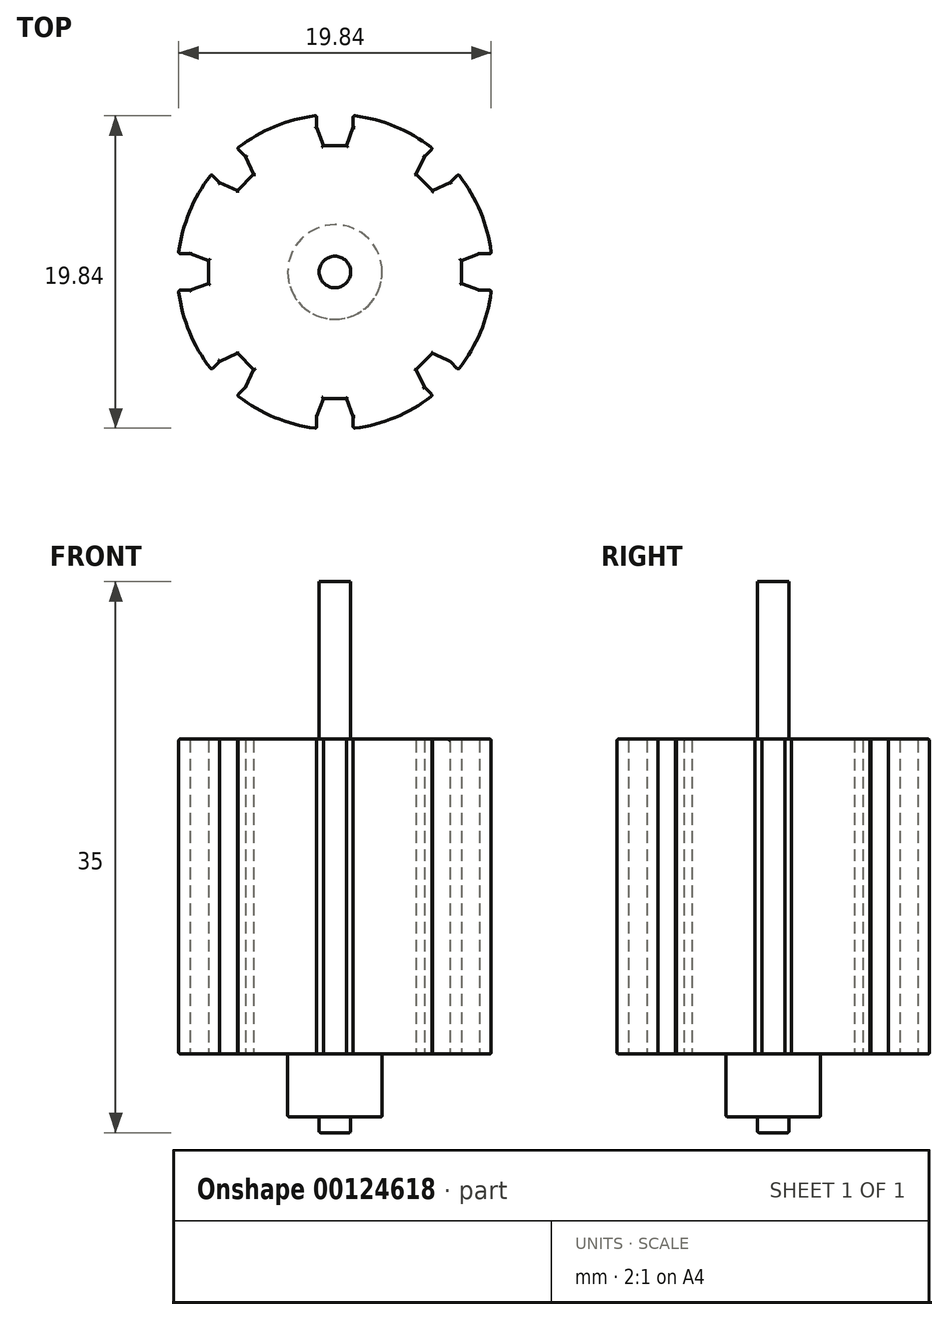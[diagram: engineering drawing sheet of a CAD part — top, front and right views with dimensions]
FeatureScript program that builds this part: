
annotation { "Feature Type Name" : "Feature", "Feature Type Description" : "" }
export const myFeature = defineFeature(function(context is Context, id is Id, definition is map)
    precondition{}
    {
        {
            var Q0;
            Q0=qCreatedBy(makeId("Top.planeOp"),FACE);
            var sketch = newSketch(context, id + "F0", { "sketchPlane" : qUnion([Q0])});
            skCircle(sketch, "E0", {"center": v(0, 0) * mm, "radius": 1 * mm});
            skSolve(sketch);
        }
        {
            var Q0;
            Q0=makeQuery(id+"F0.imprint","IMPRINT",FACE,{"disambiguationData":[TD([[makeQuery(id+"F0.imprint","IMPRINT",EDGE,{"derivedFrom":sQuery(id+"F0.wireOp",EDGE,"E0")}),1.0]])]});
            extrude(context, id + "F1", {"entities" : qUnion([Q0]), "depth" : 30 * mm});
        }
        {
            var Q0;
            Q0=qCreatedBy(makeId("Top.planeOp"),FACE);
            cPlane(context, id + "F2", {"entities" : qUnion([Q0]), "cplaneType" : CPlaneType.OFFSET, "offset" : 15 * mm, "width" : 150 * mm, "height" : 150 * mm});
        }
        {
            var Q0;
            Q0=qCreatedBy(id+"F2.planeOp",FACE);
            var sketch = newSketch(context, id + "F3", { "sketchPlane" : qUnion([Q0])});
            skCircle(sketch, "E1", {"center": v(0, 0) * mm, "radius": 10 * mm});
            skLineSegment(sketch, "E2", {"start": v(0, 10) * mm, "end": v(0, 8.03) * mm});
            skLineSegment(sketch, "E3", {"start": v(0, 8.03) * mm, "end": v(0.73, 8.03) * mm});
            skLineSegment(sketch, "E4", {"start": v(0.73, 8.03) * mm, "end": v(1.42, 9.9) * mm});
            skLineSegment(sketch, "E5", {"start": v(0, 8.03) * mm, "end": v(-0.73, 8.03) * mm});
            skLineSegment(sketch, "E6", {"start": v(-0.73, 8.03) * mm, "end": v(-1.42, 9.9) * mm});
            skLineSegment(sketch, "E7", {"start": v(1.16, 9.93) * mm, "end": v(1.16, 9.2) * mm});
            skLineSegment(sketch, "E8", {"start": v(-1.16, 9.93) * mm, "end": v(-1.16, 9.2) * mm});
            skLineSegment(sketch, "E9.1.0", {"start": v(-7.84, 6.2) * mm, "end": v(-7.32, 5.68) * mm});
            skLineSegment(sketch, "E9.1.1", {"start": v(-6.2, 5.16) * mm, "end": v(-8, 6) * mm});
            skLineSegment(sketch, "E9.1.2", {"start": v(-5.68, 5.68) * mm, "end": v(-6.2, 5.16) * mm});
            skLineSegment(sketch, "E9.1.3", {"start": v(-5.68, 5.68) * mm, "end": v(-5.16, 6.2) * mm});
            skLineSegment(sketch, "E9.1.4", {"start": v(-5.16, 6.2) * mm, "end": v(-6, 8) * mm});
            skLineSegment(sketch, "E9.1.5", {"start": v(-6.2, 7.84) * mm, "end": v(-5.68, 7.32) * mm});
            skLineSegment(sketch, "E9.2.0", {"start": v(-9.93, -1.16) * mm, "end": v(-9.2, -1.16) * mm});
            skLineSegment(sketch, "E9.2.1", {"start": v(-8.03, -0.73) * mm, "end": v(-9.9, -1.42) * mm});
            skLineSegment(sketch, "E9.2.2", {"start": v(-8.03, 0) * mm, "end": v(-8.03, -0.73) * mm});
            skLineSegment(sketch, "E9.2.3", {"start": v(-8.03, 0) * mm, "end": v(-8.03, 0.73) * mm});
            skLineSegment(sketch, "E9.2.4", {"start": v(-8.03, 0.73) * mm, "end": v(-9.9, 1.42) * mm});
            skLineSegment(sketch, "E9.2.5", {"start": v(-9.93, 1.16) * mm, "end": v(-9.2, 1.16) * mm});
            skLineSegment(sketch, "E9.3.0", {"start": v(-6.2, -7.84) * mm, "end": v(-5.68, -7.32) * mm});
            skLineSegment(sketch, "E9.3.1", {"start": v(-5.16, -6.2) * mm, "end": v(-6, -8) * mm});
            skLineSegment(sketch, "E9.3.2", {"start": v(-5.68, -5.68) * mm, "end": v(-5.16, -6.2) * mm});
            skLineSegment(sketch, "E9.3.3", {"start": v(-5.68, -5.68) * mm, "end": v(-6.2, -5.16) * mm});
            skLineSegment(sketch, "E9.3.4", {"start": v(-6.2, -5.16) * mm, "end": v(-8, -6) * mm});
            skLineSegment(sketch, "E9.3.5", {"start": v(-7.84, -6.2) * mm, "end": v(-7.32, -5.68) * mm});
            skLineSegment(sketch, "E9.4.0", {"start": v(1.16, -9.93) * mm, "end": v(1.16, -9.2) * mm});
            skLineSegment(sketch, "E9.4.1", {"start": v(0.73, -8.03) * mm, "end": v(1.42, -9.9) * mm});
            skLineSegment(sketch, "E9.4.2", {"start": v(0, -8.03) * mm, "end": v(0.73, -8.03) * mm});
            skLineSegment(sketch, "E9.4.3", {"start": v(0, -8.03) * mm, "end": v(-0.73, -8.03) * mm});
            skLineSegment(sketch, "E9.4.4", {"start": v(-0.73, -8.03) * mm, "end": v(-1.42, -9.9) * mm});
            skLineSegment(sketch, "E9.4.5", {"start": v(-1.16, -9.93) * mm, "end": v(-1.16, -9.2) * mm});
            skLineSegment(sketch, "E9.5.0", {"start": v(7.84, -6.2) * mm, "end": v(7.32, -5.68) * mm});
            skLineSegment(sketch, "E9.5.1", {"start": v(6.2, -5.16) * mm, "end": v(8, -6) * mm});
            skLineSegment(sketch, "E9.5.2", {"start": v(5.68, -5.68) * mm, "end": v(6.2, -5.16) * mm});
            skLineSegment(sketch, "E9.5.3", {"start": v(5.68, -5.68) * mm, "end": v(5.16, -6.2) * mm});
            skLineSegment(sketch, "E9.5.4", {"start": v(5.16, -6.2) * mm, "end": v(6, -8) * mm});
            skLineSegment(sketch, "E9.5.5", {"start": v(6.2, -7.84) * mm, "end": v(5.68, -7.32) * mm});
            skLineSegment(sketch, "E9.6.0", {"start": v(9.93, 1.16) * mm, "end": v(9.2, 1.16) * mm});
            skLineSegment(sketch, "E9.6.1", {"start": v(8.03, 0.73) * mm, "end": v(9.9, 1.42) * mm});
            skLineSegment(sketch, "E9.6.2", {"start": v(8.03, 0) * mm, "end": v(8.03, 0.73) * mm});
            skLineSegment(sketch, "E9.6.3", {"start": v(8.03, 0) * mm, "end": v(8.03, -0.73) * mm});
            skLineSegment(sketch, "E9.6.4", {"start": v(8.03, -0.73) * mm, "end": v(9.9, -1.42) * mm});
            skLineSegment(sketch, "E9.6.5", {"start": v(9.93, -1.16) * mm, "end": v(9.2, -1.16) * mm});
            skLineSegment(sketch, "E9.7.0", {"start": v(6.2, 7.84) * mm, "end": v(5.68, 7.32) * mm});
            skLineSegment(sketch, "E9.7.1", {"start": v(5.16, 6.2) * mm, "end": v(6, 8) * mm});
            skLineSegment(sketch, "E9.7.2", {"start": v(5.68, 5.68) * mm, "end": v(5.16, 6.2) * mm});
            skLineSegment(sketch, "E9.7.3", {"start": v(5.68, 5.68) * mm, "end": v(6.2, 5.16) * mm});
            skLineSegment(sketch, "E9.7.4", {"start": v(6.2, 5.16) * mm, "end": v(8, 6) * mm});
            skLineSegment(sketch, "E9.7.5", {"start": v(7.84, 6.2) * mm, "end": v(7.32, 5.68) * mm});
            skSolve(sketch);
        }
        {
            var Q0;
            {var subQ0=sQuery(id+"F3.wireOp",EDGE,"E9.6.0");Q0=makeQuery(id+"F3.imprint","IMPRINT",FACE,{"disambiguationData":[TD([[makeQuery(id+"F3.imprint","IMPRINT",EDGE,{"derivedFrom":subQ0}),-1.0]])]});}
            var Q1;
            {var subQ3=sQuery(id+"F3.wireOp",EDGE,"E9.7.5");Q1=makeQuery(id+"F3.imprint","IMPRINT",FACE,{"disambiguationData":[TD([[makeQuery(id+"F3.imprint","IMPRINT",EDGE,{"derivedFrom":subQ3}),1.0]])]});}
            var Q2;
            {var subQ0=sQuery(id+"F3.wireOp",EDGE,"E9.7.0");Q2=makeQuery(id+"F3.imprint","IMPRINT",FACE,{"disambiguationData":[TD([[makeQuery(id+"F3.imprint","IMPRINT",EDGE,{"derivedFrom":subQ0}),-1.0]])]});}
            var Q3;
            {var subQ3=sQuery(id+"F3.wireOp",EDGE,"E7");Q3=makeQuery(id+"F3.imprint","IMPRINT",FACE,{"disambiguationData":[TD([[makeQuery(id+"F3.imprint","IMPRINT",EDGE,{"derivedFrom":subQ3}),1.0]])]});}
            var Q4;
            {var subQ3=sQuery(id+"F3.wireOp",EDGE,"E8");Q4=makeQuery(id+"F3.imprint","IMPRINT",FACE,{"disambiguationData":[TD([[makeQuery(id+"F3.imprint","IMPRINT",EDGE,{"derivedFrom":subQ3}),-1.0]])]});}
            var Q5;
            {var subQ3=sQuery(id+"F3.wireOp",EDGE,"E9.1.5");Q5=makeQuery(id+"F3.imprint","IMPRINT",FACE,{"disambiguationData":[TD([[makeQuery(id+"F3.imprint","IMPRINT",EDGE,{"derivedFrom":subQ3}),1.0]])]});}
            var Q6;
            {var subQ0=sQuery(id+"F3.wireOp",EDGE,"E9.1.0");Q6=makeQuery(id+"F3.imprint","IMPRINT",FACE,{"disambiguationData":[TD([[makeQuery(id+"F3.imprint","IMPRINT",EDGE,{"derivedFrom":subQ0}),-1.0]])]});}
            var Q7;
            {var subQ3=sQuery(id+"F3.wireOp",EDGE,"E9.2.5");Q7=makeQuery(id+"F3.imprint","IMPRINT",FACE,{"disambiguationData":[TD([[makeQuery(id+"F3.imprint","IMPRINT",EDGE,{"derivedFrom":subQ3}),1.0]])]});}
            var Q8;
            {var subQ0=sQuery(id+"F3.wireOp",EDGE,"E9.2.0");Q8=makeQuery(id+"F3.imprint","IMPRINT",FACE,{"disambiguationData":[TD([[makeQuery(id+"F3.imprint","IMPRINT",EDGE,{"derivedFrom":subQ0}),-1.0]])]});}
            var Q9;
            {var subQ3=sQuery(id+"F3.wireOp",EDGE,"E9.3.5");Q9=makeQuery(id+"F3.imprint","IMPRINT",FACE,{"disambiguationData":[TD([[makeQuery(id+"F3.imprint","IMPRINT",EDGE,{"derivedFrom":subQ3}),1.0]])]});}
            var Q10;
            {var subQ0=sQuery(id+"F3.wireOp",EDGE,"E9.3.0");Q10=makeQuery(id+"F3.imprint","IMPRINT",FACE,{"disambiguationData":[TD([[makeQuery(id+"F3.imprint","IMPRINT",EDGE,{"derivedFrom":subQ0}),-1.0]])]});}
            var Q11;
            {var subQ3=sQuery(id+"F3.wireOp",EDGE,"E9.4.5");Q11=makeQuery(id+"F3.imprint","IMPRINT",FACE,{"disambiguationData":[TD([[makeQuery(id+"F3.imprint","IMPRINT",EDGE,{"derivedFrom":subQ3}),1.0]])]});}
            var Q12;
            {var subQ0=sQuery(id+"F3.wireOp",EDGE,"E9.4.0");Q12=makeQuery(id+"F3.imprint","IMPRINT",FACE,{"disambiguationData":[TD([[makeQuery(id+"F3.imprint","IMPRINT",EDGE,{"derivedFrom":subQ0}),-1.0]])]});}
            var Q13;
            {var subQ3=sQuery(id+"F3.wireOp",EDGE,"E9.5.5");Q13=makeQuery(id+"F3.imprint","IMPRINT",FACE,{"disambiguationData":[TD([[makeQuery(id+"F3.imprint","IMPRINT",EDGE,{"derivedFrom":subQ3}),1.0]])]});}
            var Q14;
            {var subQ0=sQuery(id+"F3.wireOp",EDGE,"E9.5.0");Q14=makeQuery(id+"F3.imprint","IMPRINT",FACE,{"disambiguationData":[TD([[makeQuery(id+"F3.imprint","IMPRINT",EDGE,{"derivedFrom":subQ0}),-1.0]])]});}
            var Q15;
            {var subQ3=sQuery(id+"F3.wireOp",EDGE,"E9.6.5");Q15=makeQuery(id+"F3.imprint","IMPRINT",FACE,{"disambiguationData":[TD([[makeQuery(id+"F3.imprint","IMPRINT",EDGE,{"derivedFrom":subQ3}),1.0]])]});}
            var Q16;
            {var subQ53=sQuery(id+"F3.wireOp",EDGE,"E3");Q16=makeQuery(id+"F3.imprint","IMPRINT",FACE,{"disambiguationData":[TD([[makeQuery(id+"F3.imprint","IMPRINT",EDGE,{"derivedFrom":subQ53}),-1.0]])]});}
            extrude(context, id + "F4", {"entities" : qUnion([Q0, Q1, Q2, Q3, Q4, Q5, Q6, Q7, Q8, Q9, Q10, Q11, Q12, Q13, Q14, Q15, Q16]), "operationType" : NewBodyOperationType.ADD, "depth" : 10 * mm});
        }
        {
            var Q0;
            Q0=makeQuery(id+"F4.opExtrude","CAP_FACE",FACE,{"disambiguationData":[OSD([sQuery(id+"F3.wireOp",EDGE,"E1"),sQuery(id+"F3.wireOp",EDGE,"E3"),sQuery(id+"F3.wireOp",EDGE,"E4"),sQuery(id+"F3.wireOp",EDGE,"E5"),sQuery(id+"F3.wireOp",EDGE,"E6"),sQuery(id+"F3.wireOp",EDGE,"E7"),sQuery(id+"F3.wireOp",EDGE,"E8"),sQuery(id+"F3.wireOp",EDGE,"E9.1.0"),sQuery(id+"F3.wireOp",EDGE,"E9.1.1"),sQuery(id+"F3.wireOp",EDGE,"E9.1.2"),sQuery(id+"F3.wireOp",EDGE,"E9.1.3"),sQuery(id+"F3.wireOp",EDGE,"E9.1.4"),sQuery(id+"F3.wireOp",EDGE,"E9.1.5"),sQuery(id+"F3.wireOp",EDGE,"E9.2.0"),sQuery(id+"F3.wireOp",EDGE,"E9.2.1"),sQuery(id+"F3.wireOp",EDGE,"E9.2.2"),sQuery(id+"F3.wireOp",EDGE,"E9.2.3"),sQuery(id+"F3.wireOp",EDGE,"E9.2.4"),sQuery(id+"F3.wireOp",EDGE,"E9.2.5"),sQuery(id+"F3.wireOp",EDGE,"E9.3.0"),sQuery(id+"F3.wireOp",EDGE,"E9.3.1"),sQuery(id+"F3.wireOp",EDGE,"E9.3.2"),sQuery(id+"F3.wireOp",EDGE,"E9.3.3"),sQuery(id+"F3.wireOp",EDGE,"E9.3.4"),sQuery(id+"F3.wireOp",EDGE,"E9.3.5"),sQuery(id+"F3.wireOp",EDGE,"E9.4.0"),sQuery(id+"F3.wireOp",EDGE,"E9.4.1"),sQuery(id+"F3.wireOp",EDGE,"E9.4.2"),sQuery(id+"F3.wireOp",EDGE,"E9.4.3"),sQuery(id+"F3.wireOp",EDGE,"E9.4.4"),sQuery(id+"F3.wireOp",EDGE,"E9.4.5"),sQuery(id+"F3.wireOp",EDGE,"E9.5.0"),sQuery(id+"F3.wireOp",EDGE,"E9.5.1"),sQuery(id+"F3.wireOp",EDGE,"E9.5.2"),sQuery(id+"F3.wireOp",EDGE,"E9.5.3"),sQuery(id+"F3.wireOp",EDGE,"E9.5.4"),sQuery(id+"F3.wireOp",EDGE,"E9.5.5"),sQuery(id+"F3.wireOp",EDGE,"E9.6.0"),sQuery(id+"F3.wireOp",EDGE,"E9.6.1"),sQuery(id+"F3.wireOp",EDGE,"E9.6.2"),sQuery(id+"F3.wireOp",EDGE,"E9.6.3"),sQuery(id+"F3.wireOp",EDGE,"E9.6.4"),sQuery(id+"F3.wireOp",EDGE,"E9.6.5"),sQuery(id+"F3.wireOp",EDGE,"E9.7.0"),sQuery(id+"F3.wireOp",EDGE,"E9.7.1"),sQuery(id+"F3.wireOp",EDGE,"E9.7.2"),sQuery(id+"F3.wireOp",EDGE,"E9.7.3"),sQuery(id+"F3.wireOp",EDGE,"E9.7.4"),sQuery(id+"F3.wireOp",EDGE,"E9.7.5")])],"isStart":true});
            extrude(context, id + "F5", {"entities" : qUnion([Q0]), "operationType" : NewBodyOperationType.ADD, "depth" : 10 * mm});
        }
        {
            var Q0;
            Q0=makeQuery(id+"F5.opExtrude","CAP_FACE",FACE,{"disambiguationData":[OSD([sQuery(id+"F3.wireOp",EDGE,"E1"),sQuery(id+"F3.wireOp",EDGE,"E3"),sQuery(id+"F3.wireOp",EDGE,"E4"),sQuery(id+"F3.wireOp",EDGE,"E5"),sQuery(id+"F3.wireOp",EDGE,"E6"),sQuery(id+"F3.wireOp",EDGE,"E7"),sQuery(id+"F3.wireOp",EDGE,"E8"),sQuery(id+"F3.wireOp",EDGE,"E9.1.0"),sQuery(id+"F3.wireOp",EDGE,"E9.1.1"),sQuery(id+"F3.wireOp",EDGE,"E9.1.2"),sQuery(id+"F3.wireOp",EDGE,"E9.1.3"),sQuery(id+"F3.wireOp",EDGE,"E9.1.4"),sQuery(id+"F3.wireOp",EDGE,"E9.1.5"),sQuery(id+"F3.wireOp",EDGE,"E9.2.0"),sQuery(id+"F3.wireOp",EDGE,"E9.2.1"),sQuery(id+"F3.wireOp",EDGE,"E9.2.2"),sQuery(id+"F3.wireOp",EDGE,"E9.2.3"),sQuery(id+"F3.wireOp",EDGE,"E9.2.4"),sQuery(id+"F3.wireOp",EDGE,"E9.2.5"),sQuery(id+"F3.wireOp",EDGE,"E9.3.0"),sQuery(id+"F3.wireOp",EDGE,"E9.3.1"),sQuery(id+"F3.wireOp",EDGE,"E9.3.2"),sQuery(id+"F3.wireOp",EDGE,"E9.3.3"),sQuery(id+"F3.wireOp",EDGE,"E9.3.4"),sQuery(id+"F3.wireOp",EDGE,"E9.3.5"),sQuery(id+"F3.wireOp",EDGE,"E9.4.0"),sQuery(id+"F3.wireOp",EDGE,"E9.4.1"),sQuery(id+"F3.wireOp",EDGE,"E9.4.2"),sQuery(id+"F3.wireOp",EDGE,"E9.4.3"),sQuery(id+"F3.wireOp",EDGE,"E9.4.4"),sQuery(id+"F3.wireOp",EDGE,"E9.4.5"),sQuery(id+"F3.wireOp",EDGE,"E9.5.0"),sQuery(id+"F3.wireOp",EDGE,"E9.5.1"),sQuery(id+"F3.wireOp",EDGE,"E9.5.2"),sQuery(id+"F3.wireOp",EDGE,"E9.5.3"),sQuery(id+"F3.wireOp",EDGE,"E9.5.4"),sQuery(id+"F3.wireOp",EDGE,"E9.5.5"),sQuery(id+"F3.wireOp",EDGE,"E9.6.0"),sQuery(id+"F3.wireOp",EDGE,"E9.6.1"),sQuery(id+"F3.wireOp",EDGE,"E9.6.2"),sQuery(id+"F3.wireOp",EDGE,"E9.6.3"),sQuery(id+"F3.wireOp",EDGE,"E9.6.4"),sQuery(id+"F3.wireOp",EDGE,"E9.6.5"),sQuery(id+"F3.wireOp",EDGE,"E9.7.0"),sQuery(id+"F3.wireOp",EDGE,"E9.7.1"),sQuery(id+"F3.wireOp",EDGE,"E9.7.2"),sQuery(id+"F3.wireOp",EDGE,"E9.7.3"),sQuery(id+"F3.wireOp",EDGE,"E9.7.4"),sQuery(id+"F3.wireOp",EDGE,"E9.7.5")])],"isStart":false});
            var sketch = newSketch(context, id + "F6", { "sketchPlane" : qUnion([Q0])});
            skCircle(sketch, "E10", {"center": v(0, 0) * mm, "radius": 3 * mm});
            skSolve(sketch);
        }
        {
            var Q0;
            Q0=makeQuery(id+"F6.imprint","IMPRINT",FACE,{"disambiguationData":[TD([[makeQuery(id+"F6.imprint","IMPRINT",EDGE,{"derivedFrom":sQuery(id+"F6.wireOp",EDGE,"E10")}),1.0]])]});
            extrude(context, id + "F7", {"entities" : qUnion([Q0]), "operationType" : NewBodyOperationType.ADD, "depth" : 4 * mm});
        }
        {
            var Q0;
            {var subQ0=sQuery(id+"F3.wireOp",EDGE,"E8");var subQ1=sQuery(id+"F3.wireOp",EDGE,"E1");Q0=makeQuery(id+"F5.boolean.opBoolean","MERGE",EDGE,{"derivedFrom":[makeQuery(id+"F4.opExtrude","SWEPT_EDGE",EDGE,{"disambiguationData":[OSD([subQ1,subQ0])]}),makeQuery(id+"F5.opExtrude","SWEPT_EDGE",EDGE,{"disambiguationData":[OSD([subQ1,subQ0])]})]});}
            var Q1;
            {var subQ0=sQuery(id+"F3.wireOp",EDGE,"E9.1.5");var subQ1=sQuery(id+"F3.wireOp",EDGE,"E1");Q1=makeQuery(id+"F5.boolean.opBoolean","MERGE",EDGE,{"derivedFrom":[makeQuery(id+"F4.opExtrude","SWEPT_EDGE",EDGE,{"disambiguationData":[OSD([subQ1,subQ0])]}),makeQuery(id+"F5.opExtrude","SWEPT_EDGE",EDGE,{"disambiguationData":[OSD([subQ1,subQ0])]})]});}
            var Q2;
            {var subQ0=sQuery(id+"F3.wireOp",EDGE,"E9.1.0");var subQ1=sQuery(id+"F3.wireOp",EDGE,"E1");Q2=makeQuery(id+"F5.boolean.opBoolean","MERGE",EDGE,{"derivedFrom":[makeQuery(id+"F4.opExtrude","SWEPT_EDGE",EDGE,{"disambiguationData":[OSD([subQ1,subQ0])]}),makeQuery(id+"F5.opExtrude","SWEPT_EDGE",EDGE,{"disambiguationData":[OSD([subQ1,subQ0])]})]});}
            var Q3;
            {var subQ0=sQuery(id+"F3.wireOp",EDGE,"E9.2.5");var subQ1=sQuery(id+"F3.wireOp",EDGE,"E1");Q3=makeQuery(id+"F5.boolean.opBoolean","MERGE",EDGE,{"derivedFrom":[makeQuery(id+"F4.opExtrude","SWEPT_EDGE",EDGE,{"disambiguationData":[OSD([subQ1,subQ0])]}),makeQuery(id+"F5.opExtrude","SWEPT_EDGE",EDGE,{"disambiguationData":[OSD([subQ1,subQ0])]})]});}
            var Q4;
            {var subQ0=sQuery(id+"F3.wireOp",EDGE,"E9.2.0");var subQ1=sQuery(id+"F3.wireOp",EDGE,"E1");Q4=makeQuery(id+"F5.boolean.opBoolean","MERGE",EDGE,{"derivedFrom":[makeQuery(id+"F4.opExtrude","SWEPT_EDGE",EDGE,{"disambiguationData":[OSD([subQ1,subQ0])]}),makeQuery(id+"F5.opExtrude","SWEPT_EDGE",EDGE,{"disambiguationData":[OSD([subQ1,subQ0])]})]});}
            var Q5;
            {var subQ0=sQuery(id+"F3.wireOp",EDGE,"E9.3.5");var subQ1=sQuery(id+"F3.wireOp",EDGE,"E1");Q5=makeQuery(id+"F5.boolean.opBoolean","MERGE",EDGE,{"derivedFrom":[makeQuery(id+"F4.opExtrude","SWEPT_EDGE",EDGE,{"disambiguationData":[OSD([subQ1,subQ0])]}),makeQuery(id+"F5.opExtrude","SWEPT_EDGE",EDGE,{"disambiguationData":[OSD([subQ1,subQ0])]})]});}
            var Q6;
            {var subQ0=sQuery(id+"F3.wireOp",EDGE,"E9.3.0");var subQ1=sQuery(id+"F3.wireOp",EDGE,"E1");Q6=makeQuery(id+"F5.boolean.opBoolean","MERGE",EDGE,{"derivedFrom":[makeQuery(id+"F4.opExtrude","SWEPT_EDGE",EDGE,{"disambiguationData":[OSD([subQ1,subQ0])]}),makeQuery(id+"F5.opExtrude","SWEPT_EDGE",EDGE,{"disambiguationData":[OSD([subQ1,subQ0])]})]});}
            var Q7;
            {var subQ0=sQuery(id+"F3.wireOp",EDGE,"E9.4.5");var subQ1=sQuery(id+"F3.wireOp",EDGE,"E1");Q7=makeQuery(id+"F5.boolean.opBoolean","MERGE",EDGE,{"derivedFrom":[makeQuery(id+"F4.opExtrude","SWEPT_EDGE",EDGE,{"disambiguationData":[OSD([subQ1,subQ0])]}),makeQuery(id+"F5.opExtrude","SWEPT_EDGE",EDGE,{"disambiguationData":[OSD([subQ1,subQ0])]})]});}
            var Q8;
            {var subQ0=sQuery(id+"F3.wireOp",EDGE,"E9.4.0");var subQ1=sQuery(id+"F3.wireOp",EDGE,"E1");Q8=makeQuery(id+"F5.boolean.opBoolean","MERGE",EDGE,{"derivedFrom":[makeQuery(id+"F4.opExtrude","SWEPT_EDGE",EDGE,{"disambiguationData":[OSD([subQ1,subQ0])]}),makeQuery(id+"F5.opExtrude","SWEPT_EDGE",EDGE,{"disambiguationData":[OSD([subQ1,subQ0])]})]});}
            var Q9;
            {var subQ0=sQuery(id+"F3.wireOp",EDGE,"E9.5.5");var subQ1=sQuery(id+"F3.wireOp",EDGE,"E1");Q9=makeQuery(id+"F5.boolean.opBoolean","MERGE",EDGE,{"derivedFrom":[makeQuery(id+"F4.opExtrude","SWEPT_EDGE",EDGE,{"disambiguationData":[OSD([subQ1,subQ0])]}),makeQuery(id+"F5.opExtrude","SWEPT_EDGE",EDGE,{"disambiguationData":[OSD([subQ1,subQ0])]})]});}
            var Q10;
            {var subQ0=sQuery(id+"F3.wireOp",EDGE,"E9.5.0");var subQ1=sQuery(id+"F3.wireOp",EDGE,"E1");Q10=makeQuery(id+"F5.boolean.opBoolean","MERGE",EDGE,{"derivedFrom":[makeQuery(id+"F4.opExtrude","SWEPT_EDGE",EDGE,{"disambiguationData":[OSD([subQ1,subQ0])]}),makeQuery(id+"F5.opExtrude","SWEPT_EDGE",EDGE,{"disambiguationData":[OSD([subQ1,subQ0])]})]});}
            var Q11;
            {var subQ0=sQuery(id+"F3.wireOp",EDGE,"E9.6.5");var subQ1=sQuery(id+"F3.wireOp",EDGE,"E1");Q11=makeQuery(id+"F5.boolean.opBoolean","MERGE",EDGE,{"derivedFrom":[makeQuery(id+"F4.opExtrude","SWEPT_EDGE",EDGE,{"disambiguationData":[OSD([subQ1,subQ0])]}),makeQuery(id+"F5.opExtrude","SWEPT_EDGE",EDGE,{"disambiguationData":[OSD([subQ1,subQ0])]})]});}
            var Q12;
            {var subQ0=sQuery(id+"F3.wireOp",EDGE,"E9.6.0");var subQ1=sQuery(id+"F3.wireOp",EDGE,"E1");Q12=makeQuery(id+"F5.boolean.opBoolean","MERGE",EDGE,{"derivedFrom":[makeQuery(id+"F4.opExtrude","SWEPT_EDGE",EDGE,{"disambiguationData":[OSD([subQ1,subQ0])]}),makeQuery(id+"F5.opExtrude","SWEPT_EDGE",EDGE,{"disambiguationData":[OSD([subQ1,subQ0])]})]});}
            var Q13;
            {var subQ0=sQuery(id+"F3.wireOp",EDGE,"E9.7.5");var subQ1=sQuery(id+"F3.wireOp",EDGE,"E1");Q13=makeQuery(id+"F5.boolean.opBoolean","MERGE",EDGE,{"derivedFrom":[makeQuery(id+"F4.opExtrude","SWEPT_EDGE",EDGE,{"disambiguationData":[OSD([subQ1,subQ0])]}),makeQuery(id+"F5.opExtrude","SWEPT_EDGE",EDGE,{"disambiguationData":[OSD([subQ1,subQ0])]})]});}
            var Q14;
            {var subQ0=sQuery(id+"F3.wireOp",EDGE,"E9.7.0");var subQ1=sQuery(id+"F3.wireOp",EDGE,"E1");Q14=makeQuery(id+"F5.boolean.opBoolean","MERGE",EDGE,{"derivedFrom":[makeQuery(id+"F4.opExtrude","SWEPT_EDGE",EDGE,{"disambiguationData":[OSD([subQ1,subQ0])]}),makeQuery(id+"F5.opExtrude","SWEPT_EDGE",EDGE,{"disambiguationData":[OSD([subQ1,subQ0])]})]});}
            var Q15;
            {var subQ0=sQuery(id+"F3.wireOp",EDGE,"E7");var subQ1=sQuery(id+"F3.wireOp",EDGE,"E1");Q15=makeQuery(id+"F5.boolean.opBoolean","MERGE",EDGE,{"derivedFrom":[makeQuery(id+"F4.opExtrude","SWEPT_EDGE",EDGE,{"disambiguationData":[OSD([subQ1,subQ0])]}),makeQuery(id+"F5.opExtrude","SWEPT_EDGE",EDGE,{"disambiguationData":[OSD([subQ1,subQ0])]})]});}
            fillet(context, id + "F8", {"entities" : qUnion([Q0, Q1, Q2, Q3, Q4, Q5, Q6, Q7, Q8, Q9, Q10, Q11, Q12, Q13, Q14, Q15]), "radius" : 0.1 * mm, "tangentPropagation" : true, "allowEdgeOverflow" : false});
        }
        {
            var Q0;
            {var subQ0=sQuery(id+"F3.wireOp",EDGE,"E1");var subQ1=makeQuery(id+"F3.imprint","INTERSECT",VERTEX,{"derivedFrom":[subQ0,sQuery(id+"F3.wireOp",EDGE,"E9.7.4")]});var subQ2=makeQuery(id+"F3.imprint","INTERSECT",VERTEX,{"derivedFrom":[subQ0,sQuery(id+"F3.wireOp",EDGE,"E9.6.1")]});Q0=makeQuery(id+"F4.opExtrude","CAP_EDGE",EDGE,{"disambiguationData":[OSD([subQ0]),TDD([makeQuery(id+"F3.imprint","IMPRINT",EDGE,{"disambiguationData":[TD([[makeQuery(id+"F3.imprint","INTERSECT",VERTEX,{"derivedFrom":[subQ0,sQuery(id+"F3.wireOp",EDGE,"E9.6.0")]}),-1.0]])],"derivedFrom":subQ0}),makeQuery(id+"F3.imprint","IMPRINT",EDGE,{"disambiguationData":[TD([[subQ2,-1.0]])],"derivedFrom":subQ0}),makeQuery(id+"F3.imprint","IMPRINT",EDGE,{"disambiguationData":[TD([[subQ1,-1.0]])],"derivedFrom":subQ0})])],"isStart":false});}
            var Q1;
            Q1=makeQuery(id+"F4.opExtrude","CAP_EDGE",EDGE,{"disambiguationData":[OSD([sQuery(id+"F3.wireOp",EDGE,"E9.6.0")])],"isStart":false});
            var Q2;
            {var subQ0=sQuery(id+"F3.wireOp",EDGE,"E9.6.0");var subQ1=sQuery(id+"F3.wireOp",EDGE,"E1");Q2=makeQuery(id+"F8.opFillet","BLEND_EDGE",EDGE,{"blendedFrom":[makeQuery(id+"F5.boolean.opBoolean","MERGE",EDGE,{"derivedFrom":[makeQuery(id+"F4.opExtrude","SWEPT_EDGE",EDGE,{"disambiguationData":[OSD([subQ1,subQ0])]}),makeQuery(id+"F5.opExtrude","SWEPT_EDGE",EDGE,{"disambiguationData":[OSD([subQ1,subQ0])]})]}),makeQuery(id+"F4.opExtrude","CAP_FACE",FACE,{"disambiguationData":[OSD([subQ1,sQuery(id+"F3.wireOp",EDGE,"E3"),sQuery(id+"F3.wireOp",EDGE,"E4"),sQuery(id+"F3.wireOp",EDGE,"E5"),sQuery(id+"F3.wireOp",EDGE,"E6"),sQuery(id+"F3.wireOp",EDGE,"E7"),sQuery(id+"F3.wireOp",EDGE,"E8"),sQuery(id+"F3.wireOp",EDGE,"E9.1.0"),sQuery(id+"F3.wireOp",EDGE,"E9.1.1"),sQuery(id+"F3.wireOp",EDGE,"E9.1.2"),sQuery(id+"F3.wireOp",EDGE,"E9.1.3"),sQuery(id+"F3.wireOp",EDGE,"E9.1.4"),sQuery(id+"F3.wireOp",EDGE,"E9.1.5"),sQuery(id+"F3.wireOp",EDGE,"E9.2.0"),sQuery(id+"F3.wireOp",EDGE,"E9.2.1"),sQuery(id+"F3.wireOp",EDGE,"E9.2.2"),sQuery(id+"F3.wireOp",EDGE,"E9.2.3"),sQuery(id+"F3.wireOp",EDGE,"E9.2.4"),sQuery(id+"F3.wireOp",EDGE,"E9.2.5"),sQuery(id+"F3.wireOp",EDGE,"E9.3.0"),sQuery(id+"F3.wireOp",EDGE,"E9.3.1"),sQuery(id+"F3.wireOp",EDGE,"E9.3.2"),sQuery(id+"F3.wireOp",EDGE,"E9.3.3"),sQuery(id+"F3.wireOp",EDGE,"E9.3.4"),sQuery(id+"F3.wireOp",EDGE,"E9.3.5"),sQuery(id+"F3.wireOp",EDGE,"E9.4.0"),sQuery(id+"F3.wireOp",EDGE,"E9.4.1"),sQuery(id+"F3.wireOp",EDGE,"E9.4.2"),sQuery(id+"F3.wireOp",EDGE,"E9.4.3"),sQuery(id+"F3.wireOp",EDGE,"E9.4.4"),sQuery(id+"F3.wireOp",EDGE,"E9.4.5"),sQuery(id+"F3.wireOp",EDGE,"E9.5.0"),sQuery(id+"F3.wireOp",EDGE,"E9.5.1"),sQuery(id+"F3.wireOp",EDGE,"E9.5.2"),sQuery(id+"F3.wireOp",EDGE,"E9.5.3"),sQuery(id+"F3.wireOp",EDGE,"E9.5.4"),sQuery(id+"F3.wireOp",EDGE,"E9.5.5"),subQ0,sQuery(id+"F3.wireOp",EDGE,"E9.6.1"),sQuery(id+"F3.wireOp",EDGE,"E9.6.2"),sQuery(id+"F3.wireOp",EDGE,"E9.6.3"),sQuery(id+"F3.wireOp",EDGE,"E9.6.4"),sQuery(id+"F3.wireOp",EDGE,"E9.6.5"),sQuery(id+"F3.wireOp",EDGE,"E9.7.0"),sQuery(id+"F3.wireOp",EDGE,"E9.7.1"),sQuery(id+"F3.wireOp",EDGE,"E9.7.2"),sQuery(id+"F3.wireOp",EDGE,"E9.7.3"),sQuery(id+"F3.wireOp",EDGE,"E9.7.4"),sQuery(id+"F3.wireOp",EDGE,"E9.7.5")])],"isStart":false})],"blendedInto":[makeQuery(id+"F4.opExtrude","CAP_FACE",FACE,{"disambiguationData":[OSD([subQ1,sQuery(id+"F3.wireOp",EDGE,"E3"),sQuery(id+"F3.wireOp",EDGE,"E4"),sQuery(id+"F3.wireOp",EDGE,"E5"),sQuery(id+"F3.wireOp",EDGE,"E6"),sQuery(id+"F3.wireOp",EDGE,"E7"),sQuery(id+"F3.wireOp",EDGE,"E8"),sQuery(id+"F3.wireOp",EDGE,"E9.1.0"),sQuery(id+"F3.wireOp",EDGE,"E9.1.1"),sQuery(id+"F3.wireOp",EDGE,"E9.1.2"),sQuery(id+"F3.wireOp",EDGE,"E9.1.3"),sQuery(id+"F3.wireOp",EDGE,"E9.1.4"),sQuery(id+"F3.wireOp",EDGE,"E9.1.5"),sQuery(id+"F3.wireOp",EDGE,"E9.2.0"),sQuery(id+"F3.wireOp",EDGE,"E9.2.1"),sQuery(id+"F3.wireOp",EDGE,"E9.2.2"),sQuery(id+"F3.wireOp",EDGE,"E9.2.3"),sQuery(id+"F3.wireOp",EDGE,"E9.2.4"),sQuery(id+"F3.wireOp",EDGE,"E9.2.5"),sQuery(id+"F3.wireOp",EDGE,"E9.3.0"),sQuery(id+"F3.wireOp",EDGE,"E9.3.1"),sQuery(id+"F3.wireOp",EDGE,"E9.3.2"),sQuery(id+"F3.wireOp",EDGE,"E9.3.3"),sQuery(id+"F3.wireOp",EDGE,"E9.3.4"),sQuery(id+"F3.wireOp",EDGE,"E9.3.5"),sQuery(id+"F3.wireOp",EDGE,"E9.4.0"),sQuery(id+"F3.wireOp",EDGE,"E9.4.1"),sQuery(id+"F3.wireOp",EDGE,"E9.4.2"),sQuery(id+"F3.wireOp",EDGE,"E9.4.3"),sQuery(id+"F3.wireOp",EDGE,"E9.4.4"),sQuery(id+"F3.wireOp",EDGE,"E9.4.5"),sQuery(id+"F3.wireOp",EDGE,"E9.5.0"),sQuery(id+"F3.wireOp",EDGE,"E9.5.1"),sQuery(id+"F3.wireOp",EDGE,"E9.5.2"),sQuery(id+"F3.wireOp",EDGE,"E9.5.3"),sQuery(id+"F3.wireOp",EDGE,"E9.5.4"),sQuery(id+"F3.wireOp",EDGE,"E9.5.5"),subQ0,sQuery(id+"F3.wireOp",EDGE,"E9.6.1"),sQuery(id+"F3.wireOp",EDGE,"E9.6.2"),sQuery(id+"F3.wireOp",EDGE,"E9.6.3"),sQuery(id+"F3.wireOp",EDGE,"E9.6.4"),sQuery(id+"F3.wireOp",EDGE,"E9.6.5"),sQuery(id+"F3.wireOp",EDGE,"E9.7.0"),sQuery(id+"F3.wireOp",EDGE,"E9.7.1"),sQuery(id+"F3.wireOp",EDGE,"E9.7.2"),sQuery(id+"F3.wireOp",EDGE,"E9.7.3"),sQuery(id+"F3.wireOp",EDGE,"E9.7.4"),sQuery(id+"F3.wireOp",EDGE,"E9.7.5")])],"isStart":false})]});}
            var Q3;
            Q3=makeQuery(id+"F4.opExtrude","CAP_EDGE",EDGE,{"disambiguationData":[OSD([sQuery(id+"F3.wireOp",EDGE,"E9.6.1")])],"isStart":false});
            var Q4;
            Q4=makeQuery(id+"F4.opExtrude","CAP_EDGE",EDGE,{"disambiguationData":[OSD([sQuery(id+"F3.wireOp",EDGE,"E9.6.2"),sQuery(id+"F3.wireOp",EDGE,"E9.6.3")])],"isStart":false});
            var Q5;
            Q5=makeQuery(id+"F4.opExtrude","CAP_EDGE",EDGE,{"disambiguationData":[OSD([sQuery(id+"F3.wireOp",EDGE,"E9.6.4")])],"isStart":false});
            var Q6;
            Q6=makeQuery(id+"F4.opExtrude","CAP_EDGE",EDGE,{"disambiguationData":[OSD([sQuery(id+"F3.wireOp",EDGE,"E9.6.5")])],"isStart":false});
            var Q7;
            {var subQ0=sQuery(id+"F3.wireOp",EDGE,"E9.6.5");var subQ1=sQuery(id+"F3.wireOp",EDGE,"E1");Q7=makeQuery(id+"F8.opFillet","BLEND_EDGE",EDGE,{"blendedFrom":[makeQuery(id+"F5.boolean.opBoolean","MERGE",EDGE,{"derivedFrom":[makeQuery(id+"F4.opExtrude","SWEPT_EDGE",EDGE,{"disambiguationData":[OSD([subQ1,subQ0])]}),makeQuery(id+"F5.opExtrude","SWEPT_EDGE",EDGE,{"disambiguationData":[OSD([subQ1,subQ0])]})]}),makeQuery(id+"F4.opExtrude","CAP_FACE",FACE,{"disambiguationData":[OSD([subQ1,sQuery(id+"F3.wireOp",EDGE,"E3"),sQuery(id+"F3.wireOp",EDGE,"E4"),sQuery(id+"F3.wireOp",EDGE,"E5"),sQuery(id+"F3.wireOp",EDGE,"E6"),sQuery(id+"F3.wireOp",EDGE,"E7"),sQuery(id+"F3.wireOp",EDGE,"E8"),sQuery(id+"F3.wireOp",EDGE,"E9.1.0"),sQuery(id+"F3.wireOp",EDGE,"E9.1.1"),sQuery(id+"F3.wireOp",EDGE,"E9.1.2"),sQuery(id+"F3.wireOp",EDGE,"E9.1.3"),sQuery(id+"F3.wireOp",EDGE,"E9.1.4"),sQuery(id+"F3.wireOp",EDGE,"E9.1.5"),sQuery(id+"F3.wireOp",EDGE,"E9.2.0"),sQuery(id+"F3.wireOp",EDGE,"E9.2.1"),sQuery(id+"F3.wireOp",EDGE,"E9.2.2"),sQuery(id+"F3.wireOp",EDGE,"E9.2.3"),sQuery(id+"F3.wireOp",EDGE,"E9.2.4"),sQuery(id+"F3.wireOp",EDGE,"E9.2.5"),sQuery(id+"F3.wireOp",EDGE,"E9.3.0"),sQuery(id+"F3.wireOp",EDGE,"E9.3.1"),sQuery(id+"F3.wireOp",EDGE,"E9.3.2"),sQuery(id+"F3.wireOp",EDGE,"E9.3.3"),sQuery(id+"F3.wireOp",EDGE,"E9.3.4"),sQuery(id+"F3.wireOp",EDGE,"E9.3.5"),sQuery(id+"F3.wireOp",EDGE,"E9.4.0"),sQuery(id+"F3.wireOp",EDGE,"E9.4.1"),sQuery(id+"F3.wireOp",EDGE,"E9.4.2"),sQuery(id+"F3.wireOp",EDGE,"E9.4.3"),sQuery(id+"F3.wireOp",EDGE,"E9.4.4"),sQuery(id+"F3.wireOp",EDGE,"E9.4.5"),sQuery(id+"F3.wireOp",EDGE,"E9.5.0"),sQuery(id+"F3.wireOp",EDGE,"E9.5.1"),sQuery(id+"F3.wireOp",EDGE,"E9.5.2"),sQuery(id+"F3.wireOp",EDGE,"E9.5.3"),sQuery(id+"F3.wireOp",EDGE,"E9.5.4"),sQuery(id+"F3.wireOp",EDGE,"E9.5.5"),sQuery(id+"F3.wireOp",EDGE,"E9.6.0"),sQuery(id+"F3.wireOp",EDGE,"E9.6.1"),sQuery(id+"F3.wireOp",EDGE,"E9.6.2"),sQuery(id+"F3.wireOp",EDGE,"E9.6.3"),sQuery(id+"F3.wireOp",EDGE,"E9.6.4"),subQ0,sQuery(id+"F3.wireOp",EDGE,"E9.7.0"),sQuery(id+"F3.wireOp",EDGE,"E9.7.1"),sQuery(id+"F3.wireOp",EDGE,"E9.7.2"),sQuery(id+"F3.wireOp",EDGE,"E9.7.3"),sQuery(id+"F3.wireOp",EDGE,"E9.7.4"),sQuery(id+"F3.wireOp",EDGE,"E9.7.5")])],"isStart":false})],"blendedInto":[makeQuery(id+"F4.opExtrude","CAP_FACE",FACE,{"disambiguationData":[OSD([subQ1,sQuery(id+"F3.wireOp",EDGE,"E3"),sQuery(id+"F3.wireOp",EDGE,"E4"),sQuery(id+"F3.wireOp",EDGE,"E5"),sQuery(id+"F3.wireOp",EDGE,"E6"),sQuery(id+"F3.wireOp",EDGE,"E7"),sQuery(id+"F3.wireOp",EDGE,"E8"),sQuery(id+"F3.wireOp",EDGE,"E9.1.0"),sQuery(id+"F3.wireOp",EDGE,"E9.1.1"),sQuery(id+"F3.wireOp",EDGE,"E9.1.2"),sQuery(id+"F3.wireOp",EDGE,"E9.1.3"),sQuery(id+"F3.wireOp",EDGE,"E9.1.4"),sQuery(id+"F3.wireOp",EDGE,"E9.1.5"),sQuery(id+"F3.wireOp",EDGE,"E9.2.0"),sQuery(id+"F3.wireOp",EDGE,"E9.2.1"),sQuery(id+"F3.wireOp",EDGE,"E9.2.2"),sQuery(id+"F3.wireOp",EDGE,"E9.2.3"),sQuery(id+"F3.wireOp",EDGE,"E9.2.4"),sQuery(id+"F3.wireOp",EDGE,"E9.2.5"),sQuery(id+"F3.wireOp",EDGE,"E9.3.0"),sQuery(id+"F3.wireOp",EDGE,"E9.3.1"),sQuery(id+"F3.wireOp",EDGE,"E9.3.2"),sQuery(id+"F3.wireOp",EDGE,"E9.3.3"),sQuery(id+"F3.wireOp",EDGE,"E9.3.4"),sQuery(id+"F3.wireOp",EDGE,"E9.3.5"),sQuery(id+"F3.wireOp",EDGE,"E9.4.0"),sQuery(id+"F3.wireOp",EDGE,"E9.4.1"),sQuery(id+"F3.wireOp",EDGE,"E9.4.2"),sQuery(id+"F3.wireOp",EDGE,"E9.4.3"),sQuery(id+"F3.wireOp",EDGE,"E9.4.4"),sQuery(id+"F3.wireOp",EDGE,"E9.4.5"),sQuery(id+"F3.wireOp",EDGE,"E9.5.0"),sQuery(id+"F3.wireOp",EDGE,"E9.5.1"),sQuery(id+"F3.wireOp",EDGE,"E9.5.2"),sQuery(id+"F3.wireOp",EDGE,"E9.5.3"),sQuery(id+"F3.wireOp",EDGE,"E9.5.4"),sQuery(id+"F3.wireOp",EDGE,"E9.5.5"),sQuery(id+"F3.wireOp",EDGE,"E9.6.0"),sQuery(id+"F3.wireOp",EDGE,"E9.6.1"),sQuery(id+"F3.wireOp",EDGE,"E9.6.2"),sQuery(id+"F3.wireOp",EDGE,"E9.6.3"),sQuery(id+"F3.wireOp",EDGE,"E9.6.4"),subQ0,sQuery(id+"F3.wireOp",EDGE,"E9.7.0"),sQuery(id+"F3.wireOp",EDGE,"E9.7.1"),sQuery(id+"F3.wireOp",EDGE,"E9.7.2"),sQuery(id+"F3.wireOp",EDGE,"E9.7.3"),sQuery(id+"F3.wireOp",EDGE,"E9.7.4"),sQuery(id+"F3.wireOp",EDGE,"E9.7.5")])],"isStart":false})]});}
            var Q8;
            {var subQ0=sQuery(id+"F3.wireOp",EDGE,"E1");var subQ1=makeQuery(id+"F3.imprint","INTERSECT",VERTEX,{"derivedFrom":[subQ0,sQuery(id+"F3.wireOp",EDGE,"E9.6.4")]});var subQ2=makeQuery(id+"F3.imprint","INTERSECT",VERTEX,{"derivedFrom":[subQ0,sQuery(id+"F3.wireOp",EDGE,"E9.5.1")]});Q8=makeQuery(id+"F4.opExtrude","CAP_EDGE",EDGE,{"disambiguationData":[OSD([subQ0]),TDD([makeQuery(id+"F3.imprint","IMPRINT",EDGE,{"disambiguationData":[TD([[makeQuery(id+"F3.imprint","INTERSECT",VERTEX,{"derivedFrom":[subQ0,sQuery(id+"F3.wireOp",EDGE,"E9.5.0")]}),-1.0]])],"derivedFrom":subQ0}),makeQuery(id+"F3.imprint","IMPRINT",EDGE,{"disambiguationData":[TD([[subQ2,-1.0]])],"derivedFrom":subQ0}),makeQuery(id+"F3.imprint","IMPRINT",EDGE,{"disambiguationData":[TD([[subQ1,-1.0]])],"derivedFrom":subQ0})])],"isStart":false});}
            var Q9;
            {var subQ0=sQuery(id+"F3.wireOp",EDGE,"E9.5.0");var subQ1=sQuery(id+"F3.wireOp",EDGE,"E1");Q9=makeQuery(id+"F8.opFillet","BLEND_EDGE",EDGE,{"blendedFrom":[makeQuery(id+"F5.boolean.opBoolean","MERGE",EDGE,{"derivedFrom":[makeQuery(id+"F4.opExtrude","SWEPT_EDGE",EDGE,{"disambiguationData":[OSD([subQ1,subQ0])]}),makeQuery(id+"F5.opExtrude","SWEPT_EDGE",EDGE,{"disambiguationData":[OSD([subQ1,subQ0])]})]}),makeQuery(id+"F4.opExtrude","CAP_FACE",FACE,{"disambiguationData":[OSD([subQ1,sQuery(id+"F3.wireOp",EDGE,"E3"),sQuery(id+"F3.wireOp",EDGE,"E4"),sQuery(id+"F3.wireOp",EDGE,"E5"),sQuery(id+"F3.wireOp",EDGE,"E6"),sQuery(id+"F3.wireOp",EDGE,"E7"),sQuery(id+"F3.wireOp",EDGE,"E8"),sQuery(id+"F3.wireOp",EDGE,"E9.1.0"),sQuery(id+"F3.wireOp",EDGE,"E9.1.1"),sQuery(id+"F3.wireOp",EDGE,"E9.1.2"),sQuery(id+"F3.wireOp",EDGE,"E9.1.3"),sQuery(id+"F3.wireOp",EDGE,"E9.1.4"),sQuery(id+"F3.wireOp",EDGE,"E9.1.5"),sQuery(id+"F3.wireOp",EDGE,"E9.2.0"),sQuery(id+"F3.wireOp",EDGE,"E9.2.1"),sQuery(id+"F3.wireOp",EDGE,"E9.2.2"),sQuery(id+"F3.wireOp",EDGE,"E9.2.3"),sQuery(id+"F3.wireOp",EDGE,"E9.2.4"),sQuery(id+"F3.wireOp",EDGE,"E9.2.5"),sQuery(id+"F3.wireOp",EDGE,"E9.3.0"),sQuery(id+"F3.wireOp",EDGE,"E9.3.1"),sQuery(id+"F3.wireOp",EDGE,"E9.3.2"),sQuery(id+"F3.wireOp",EDGE,"E9.3.3"),sQuery(id+"F3.wireOp",EDGE,"E9.3.4"),sQuery(id+"F3.wireOp",EDGE,"E9.3.5"),sQuery(id+"F3.wireOp",EDGE,"E9.4.0"),sQuery(id+"F3.wireOp",EDGE,"E9.4.1"),sQuery(id+"F3.wireOp",EDGE,"E9.4.2"),sQuery(id+"F3.wireOp",EDGE,"E9.4.3"),sQuery(id+"F3.wireOp",EDGE,"E9.4.4"),sQuery(id+"F3.wireOp",EDGE,"E9.4.5"),subQ0,sQuery(id+"F3.wireOp",EDGE,"E9.5.1"),sQuery(id+"F3.wireOp",EDGE,"E9.5.2"),sQuery(id+"F3.wireOp",EDGE,"E9.5.3"),sQuery(id+"F3.wireOp",EDGE,"E9.5.4"),sQuery(id+"F3.wireOp",EDGE,"E9.5.5"),sQuery(id+"F3.wireOp",EDGE,"E9.6.0"),sQuery(id+"F3.wireOp",EDGE,"E9.6.1"),sQuery(id+"F3.wireOp",EDGE,"E9.6.2"),sQuery(id+"F3.wireOp",EDGE,"E9.6.3"),sQuery(id+"F3.wireOp",EDGE,"E9.6.4"),sQuery(id+"F3.wireOp",EDGE,"E9.6.5"),sQuery(id+"F3.wireOp",EDGE,"E9.7.0"),sQuery(id+"F3.wireOp",EDGE,"E9.7.1"),sQuery(id+"F3.wireOp",EDGE,"E9.7.2"),sQuery(id+"F3.wireOp",EDGE,"E9.7.3"),sQuery(id+"F3.wireOp",EDGE,"E9.7.4"),sQuery(id+"F3.wireOp",EDGE,"E9.7.5")])],"isStart":false})],"blendedInto":[makeQuery(id+"F4.opExtrude","CAP_FACE",FACE,{"disambiguationData":[OSD([subQ1,sQuery(id+"F3.wireOp",EDGE,"E3"),sQuery(id+"F3.wireOp",EDGE,"E4"),sQuery(id+"F3.wireOp",EDGE,"E5"),sQuery(id+"F3.wireOp",EDGE,"E6"),sQuery(id+"F3.wireOp",EDGE,"E7"),sQuery(id+"F3.wireOp",EDGE,"E8"),sQuery(id+"F3.wireOp",EDGE,"E9.1.0"),sQuery(id+"F3.wireOp",EDGE,"E9.1.1"),sQuery(id+"F3.wireOp",EDGE,"E9.1.2"),sQuery(id+"F3.wireOp",EDGE,"E9.1.3"),sQuery(id+"F3.wireOp",EDGE,"E9.1.4"),sQuery(id+"F3.wireOp",EDGE,"E9.1.5"),sQuery(id+"F3.wireOp",EDGE,"E9.2.0"),sQuery(id+"F3.wireOp",EDGE,"E9.2.1"),sQuery(id+"F3.wireOp",EDGE,"E9.2.2"),sQuery(id+"F3.wireOp",EDGE,"E9.2.3"),sQuery(id+"F3.wireOp",EDGE,"E9.2.4"),sQuery(id+"F3.wireOp",EDGE,"E9.2.5"),sQuery(id+"F3.wireOp",EDGE,"E9.3.0"),sQuery(id+"F3.wireOp",EDGE,"E9.3.1"),sQuery(id+"F3.wireOp",EDGE,"E9.3.2"),sQuery(id+"F3.wireOp",EDGE,"E9.3.3"),sQuery(id+"F3.wireOp",EDGE,"E9.3.4"),sQuery(id+"F3.wireOp",EDGE,"E9.3.5"),sQuery(id+"F3.wireOp",EDGE,"E9.4.0"),sQuery(id+"F3.wireOp",EDGE,"E9.4.1"),sQuery(id+"F3.wireOp",EDGE,"E9.4.2"),sQuery(id+"F3.wireOp",EDGE,"E9.4.3"),sQuery(id+"F3.wireOp",EDGE,"E9.4.4"),sQuery(id+"F3.wireOp",EDGE,"E9.4.5"),subQ0,sQuery(id+"F3.wireOp",EDGE,"E9.5.1"),sQuery(id+"F3.wireOp",EDGE,"E9.5.2"),sQuery(id+"F3.wireOp",EDGE,"E9.5.3"),sQuery(id+"F3.wireOp",EDGE,"E9.5.4"),sQuery(id+"F3.wireOp",EDGE,"E9.5.5"),sQuery(id+"F3.wireOp",EDGE,"E9.6.0"),sQuery(id+"F3.wireOp",EDGE,"E9.6.1"),sQuery(id+"F3.wireOp",EDGE,"E9.6.2"),sQuery(id+"F3.wireOp",EDGE,"E9.6.3"),sQuery(id+"F3.wireOp",EDGE,"E9.6.4"),sQuery(id+"F3.wireOp",EDGE,"E9.6.5"),sQuery(id+"F3.wireOp",EDGE,"E9.7.0"),sQuery(id+"F3.wireOp",EDGE,"E9.7.1"),sQuery(id+"F3.wireOp",EDGE,"E9.7.2"),sQuery(id+"F3.wireOp",EDGE,"E9.7.3"),sQuery(id+"F3.wireOp",EDGE,"E9.7.4"),sQuery(id+"F3.wireOp",EDGE,"E9.7.5")])],"isStart":false})]});}
            var Q10;
            Q10=makeQuery(id+"F4.opExtrude","CAP_EDGE",EDGE,{"disambiguationData":[OSD([sQuery(id+"F3.wireOp",EDGE,"E9.5.0")])],"isStart":false});
            var Q11;
            {var subQ0=sQuery(id+"F3.wireOp",EDGE,"E9.5.1");var subQ1=sQuery(id+"F3.wireOp",EDGE,"E9.5.0");Q11=makeQuery(id+"F5.boolean.opBoolean","MERGE",EDGE,{"derivedFrom":[makeQuery(id+"F4.opExtrude","SWEPT_EDGE",EDGE,{"disambiguationData":[OSD([subQ1,subQ0])]}),makeQuery(id+"F5.opExtrude","SWEPT_EDGE",EDGE,{"disambiguationData":[OSD([subQ1,subQ0])]})]});}
            var Q12;
            Q12=makeQuery(id+"F4.opExtrude","CAP_EDGE",EDGE,{"disambiguationData":[OSD([sQuery(id+"F3.wireOp",EDGE,"E9.5.2"),sQuery(id+"F3.wireOp",EDGE,"E9.5.3")])],"isStart":false});
            var Q13;
            Q13=makeQuery(id+"F4.opExtrude","CAP_EDGE",EDGE,{"disambiguationData":[OSD([sQuery(id+"F3.wireOp",EDGE,"E9.5.4")])],"isStart":false});
            var Q14;
            Q14=makeQuery(id+"F4.opExtrude","CAP_EDGE",EDGE,{"disambiguationData":[OSD([sQuery(id+"F3.wireOp",EDGE,"E9.5.5")])],"isStart":false});
            var Q15;
            {var subQ0=sQuery(id+"F3.wireOp",EDGE,"E9.5.5");var subQ1=sQuery(id+"F3.wireOp",EDGE,"E1");Q15=makeQuery(id+"F8.opFillet","BLEND_EDGE",EDGE,{"blendedFrom":[makeQuery(id+"F5.boolean.opBoolean","MERGE",EDGE,{"derivedFrom":[makeQuery(id+"F4.opExtrude","SWEPT_EDGE",EDGE,{"disambiguationData":[OSD([subQ1,subQ0])]}),makeQuery(id+"F5.opExtrude","SWEPT_EDGE",EDGE,{"disambiguationData":[OSD([subQ1,subQ0])]})]}),makeQuery(id+"F4.opExtrude","CAP_FACE",FACE,{"disambiguationData":[OSD([subQ1,sQuery(id+"F3.wireOp",EDGE,"E3"),sQuery(id+"F3.wireOp",EDGE,"E4"),sQuery(id+"F3.wireOp",EDGE,"E5"),sQuery(id+"F3.wireOp",EDGE,"E6"),sQuery(id+"F3.wireOp",EDGE,"E7"),sQuery(id+"F3.wireOp",EDGE,"E8"),sQuery(id+"F3.wireOp",EDGE,"E9.1.0"),sQuery(id+"F3.wireOp",EDGE,"E9.1.1"),sQuery(id+"F3.wireOp",EDGE,"E9.1.2"),sQuery(id+"F3.wireOp",EDGE,"E9.1.3"),sQuery(id+"F3.wireOp",EDGE,"E9.1.4"),sQuery(id+"F3.wireOp",EDGE,"E9.1.5"),sQuery(id+"F3.wireOp",EDGE,"E9.2.0"),sQuery(id+"F3.wireOp",EDGE,"E9.2.1"),sQuery(id+"F3.wireOp",EDGE,"E9.2.2"),sQuery(id+"F3.wireOp",EDGE,"E9.2.3"),sQuery(id+"F3.wireOp",EDGE,"E9.2.4"),sQuery(id+"F3.wireOp",EDGE,"E9.2.5"),sQuery(id+"F3.wireOp",EDGE,"E9.3.0"),sQuery(id+"F3.wireOp",EDGE,"E9.3.1"),sQuery(id+"F3.wireOp",EDGE,"E9.3.2"),sQuery(id+"F3.wireOp",EDGE,"E9.3.3"),sQuery(id+"F3.wireOp",EDGE,"E9.3.4"),sQuery(id+"F3.wireOp",EDGE,"E9.3.5"),sQuery(id+"F3.wireOp",EDGE,"E9.4.0"),sQuery(id+"F3.wireOp",EDGE,"E9.4.1"),sQuery(id+"F3.wireOp",EDGE,"E9.4.2"),sQuery(id+"F3.wireOp",EDGE,"E9.4.3"),sQuery(id+"F3.wireOp",EDGE,"E9.4.4"),sQuery(id+"F3.wireOp",EDGE,"E9.4.5"),sQuery(id+"F3.wireOp",EDGE,"E9.5.0"),sQuery(id+"F3.wireOp",EDGE,"E9.5.1"),sQuery(id+"F3.wireOp",EDGE,"E9.5.2"),sQuery(id+"F3.wireOp",EDGE,"E9.5.3"),sQuery(id+"F3.wireOp",EDGE,"E9.5.4"),subQ0,sQuery(id+"F3.wireOp",EDGE,"E9.6.0"),sQuery(id+"F3.wireOp",EDGE,"E9.6.1"),sQuery(id+"F3.wireOp",EDGE,"E9.6.2"),sQuery(id+"F3.wireOp",EDGE,"E9.6.3"),sQuery(id+"F3.wireOp",EDGE,"E9.6.4"),sQuery(id+"F3.wireOp",EDGE,"E9.6.5"),sQuery(id+"F3.wireOp",EDGE,"E9.7.0"),sQuery(id+"F3.wireOp",EDGE,"E9.7.1"),sQuery(id+"F3.wireOp",EDGE,"E9.7.2"),sQuery(id+"F3.wireOp",EDGE,"E9.7.3"),sQuery(id+"F3.wireOp",EDGE,"E9.7.4"),sQuery(id+"F3.wireOp",EDGE,"E9.7.5")])],"isStart":false})],"blendedInto":[makeQuery(id+"F4.opExtrude","CAP_FACE",FACE,{"disambiguationData":[OSD([subQ1,sQuery(id+"F3.wireOp",EDGE,"E3"),sQuery(id+"F3.wireOp",EDGE,"E4"),sQuery(id+"F3.wireOp",EDGE,"E5"),sQuery(id+"F3.wireOp",EDGE,"E6"),sQuery(id+"F3.wireOp",EDGE,"E7"),sQuery(id+"F3.wireOp",EDGE,"E8"),sQuery(id+"F3.wireOp",EDGE,"E9.1.0"),sQuery(id+"F3.wireOp",EDGE,"E9.1.1"),sQuery(id+"F3.wireOp",EDGE,"E9.1.2"),sQuery(id+"F3.wireOp",EDGE,"E9.1.3"),sQuery(id+"F3.wireOp",EDGE,"E9.1.4"),sQuery(id+"F3.wireOp",EDGE,"E9.1.5"),sQuery(id+"F3.wireOp",EDGE,"E9.2.0"),sQuery(id+"F3.wireOp",EDGE,"E9.2.1"),sQuery(id+"F3.wireOp",EDGE,"E9.2.2"),sQuery(id+"F3.wireOp",EDGE,"E9.2.3"),sQuery(id+"F3.wireOp",EDGE,"E9.2.4"),sQuery(id+"F3.wireOp",EDGE,"E9.2.5"),sQuery(id+"F3.wireOp",EDGE,"E9.3.0"),sQuery(id+"F3.wireOp",EDGE,"E9.3.1"),sQuery(id+"F3.wireOp",EDGE,"E9.3.2"),sQuery(id+"F3.wireOp",EDGE,"E9.3.3"),sQuery(id+"F3.wireOp",EDGE,"E9.3.4"),sQuery(id+"F3.wireOp",EDGE,"E9.3.5"),sQuery(id+"F3.wireOp",EDGE,"E9.4.0"),sQuery(id+"F3.wireOp",EDGE,"E9.4.1"),sQuery(id+"F3.wireOp",EDGE,"E9.4.2"),sQuery(id+"F3.wireOp",EDGE,"E9.4.3"),sQuery(id+"F3.wireOp",EDGE,"E9.4.4"),sQuery(id+"F3.wireOp",EDGE,"E9.4.5"),sQuery(id+"F3.wireOp",EDGE,"E9.5.0"),sQuery(id+"F3.wireOp",EDGE,"E9.5.1"),sQuery(id+"F3.wireOp",EDGE,"E9.5.2"),sQuery(id+"F3.wireOp",EDGE,"E9.5.3"),sQuery(id+"F3.wireOp",EDGE,"E9.5.4"),subQ0,sQuery(id+"F3.wireOp",EDGE,"E9.6.0"),sQuery(id+"F3.wireOp",EDGE,"E9.6.1"),sQuery(id+"F3.wireOp",EDGE,"E9.6.2"),sQuery(id+"F3.wireOp",EDGE,"E9.6.3"),sQuery(id+"F3.wireOp",EDGE,"E9.6.4"),sQuery(id+"F3.wireOp",EDGE,"E9.6.5"),sQuery(id+"F3.wireOp",EDGE,"E9.7.0"),sQuery(id+"F3.wireOp",EDGE,"E9.7.1"),sQuery(id+"F3.wireOp",EDGE,"E9.7.2"),sQuery(id+"F3.wireOp",EDGE,"E9.7.3"),sQuery(id+"F3.wireOp",EDGE,"E9.7.4"),sQuery(id+"F3.wireOp",EDGE,"E9.7.5")])],"isStart":false})]});}
            var Q16;
            {var subQ0=sQuery(id+"F3.wireOp",EDGE,"E1");var subQ1=makeQuery(id+"F3.imprint","INTERSECT",VERTEX,{"derivedFrom":[subQ0,sQuery(id+"F3.wireOp",EDGE,"E9.5.4")]});var subQ2=makeQuery(id+"F3.imprint","INTERSECT",VERTEX,{"derivedFrom":[subQ0,sQuery(id+"F3.wireOp",EDGE,"E9.4.1")]});Q16=makeQuery(id+"F4.opExtrude","CAP_EDGE",EDGE,{"disambiguationData":[OSD([subQ0]),TDD([makeQuery(id+"F3.imprint","IMPRINT",EDGE,{"disambiguationData":[TD([[makeQuery(id+"F3.imprint","INTERSECT",VERTEX,{"derivedFrom":[subQ0,sQuery(id+"F3.wireOp",EDGE,"E9.4.0")]}),-1.0]])],"derivedFrom":subQ0}),makeQuery(id+"F3.imprint","IMPRINT",EDGE,{"disambiguationData":[TD([[subQ2,-1.0]])],"derivedFrom":subQ0}),makeQuery(id+"F3.imprint","IMPRINT",EDGE,{"disambiguationData":[TD([[subQ1,-1.0]])],"derivedFrom":subQ0})])],"isStart":false});}
            var Q17;
            {var subQ0=sQuery(id+"F3.wireOp",EDGE,"E9.4.0");var subQ1=sQuery(id+"F3.wireOp",EDGE,"E1");Q17=makeQuery(id+"F8.opFillet","BLEND_EDGE",EDGE,{"blendedFrom":[makeQuery(id+"F5.boolean.opBoolean","MERGE",EDGE,{"derivedFrom":[makeQuery(id+"F4.opExtrude","SWEPT_EDGE",EDGE,{"disambiguationData":[OSD([subQ1,subQ0])]}),makeQuery(id+"F5.opExtrude","SWEPT_EDGE",EDGE,{"disambiguationData":[OSD([subQ1,subQ0])]})]}),makeQuery(id+"F4.opExtrude","CAP_FACE",FACE,{"disambiguationData":[OSD([subQ1,sQuery(id+"F3.wireOp",EDGE,"E3"),sQuery(id+"F3.wireOp",EDGE,"E4"),sQuery(id+"F3.wireOp",EDGE,"E5"),sQuery(id+"F3.wireOp",EDGE,"E6"),sQuery(id+"F3.wireOp",EDGE,"E7"),sQuery(id+"F3.wireOp",EDGE,"E8"),sQuery(id+"F3.wireOp",EDGE,"E9.1.0"),sQuery(id+"F3.wireOp",EDGE,"E9.1.1"),sQuery(id+"F3.wireOp",EDGE,"E9.1.2"),sQuery(id+"F3.wireOp",EDGE,"E9.1.3"),sQuery(id+"F3.wireOp",EDGE,"E9.1.4"),sQuery(id+"F3.wireOp",EDGE,"E9.1.5"),sQuery(id+"F3.wireOp",EDGE,"E9.2.0"),sQuery(id+"F3.wireOp",EDGE,"E9.2.1"),sQuery(id+"F3.wireOp",EDGE,"E9.2.2"),sQuery(id+"F3.wireOp",EDGE,"E9.2.3"),sQuery(id+"F3.wireOp",EDGE,"E9.2.4"),sQuery(id+"F3.wireOp",EDGE,"E9.2.5"),sQuery(id+"F3.wireOp",EDGE,"E9.3.0"),sQuery(id+"F3.wireOp",EDGE,"E9.3.1"),sQuery(id+"F3.wireOp",EDGE,"E9.3.2"),sQuery(id+"F3.wireOp",EDGE,"E9.3.3"),sQuery(id+"F3.wireOp",EDGE,"E9.3.4"),sQuery(id+"F3.wireOp",EDGE,"E9.3.5"),subQ0,sQuery(id+"F3.wireOp",EDGE,"E9.4.1"),sQuery(id+"F3.wireOp",EDGE,"E9.4.2"),sQuery(id+"F3.wireOp",EDGE,"E9.4.3"),sQuery(id+"F3.wireOp",EDGE,"E9.4.4"),sQuery(id+"F3.wireOp",EDGE,"E9.4.5"),sQuery(id+"F3.wireOp",EDGE,"E9.5.0"),sQuery(id+"F3.wireOp",EDGE,"E9.5.1"),sQuery(id+"F3.wireOp",EDGE,"E9.5.2"),sQuery(id+"F3.wireOp",EDGE,"E9.5.3"),sQuery(id+"F3.wireOp",EDGE,"E9.5.4"),sQuery(id+"F3.wireOp",EDGE,"E9.5.5"),sQuery(id+"F3.wireOp",EDGE,"E9.6.0"),sQuery(id+"F3.wireOp",EDGE,"E9.6.1"),sQuery(id+"F3.wireOp",EDGE,"E9.6.2"),sQuery(id+"F3.wireOp",EDGE,"E9.6.3"),sQuery(id+"F3.wireOp",EDGE,"E9.6.4"),sQuery(id+"F3.wireOp",EDGE,"E9.6.5"),sQuery(id+"F3.wireOp",EDGE,"E9.7.0"),sQuery(id+"F3.wireOp",EDGE,"E9.7.1"),sQuery(id+"F3.wireOp",EDGE,"E9.7.2"),sQuery(id+"F3.wireOp",EDGE,"E9.7.3"),sQuery(id+"F3.wireOp",EDGE,"E9.7.4"),sQuery(id+"F3.wireOp",EDGE,"E9.7.5")])],"isStart":false})],"blendedInto":[makeQuery(id+"F4.opExtrude","CAP_FACE",FACE,{"disambiguationData":[OSD([subQ1,sQuery(id+"F3.wireOp",EDGE,"E3"),sQuery(id+"F3.wireOp",EDGE,"E4"),sQuery(id+"F3.wireOp",EDGE,"E5"),sQuery(id+"F3.wireOp",EDGE,"E6"),sQuery(id+"F3.wireOp",EDGE,"E7"),sQuery(id+"F3.wireOp",EDGE,"E8"),sQuery(id+"F3.wireOp",EDGE,"E9.1.0"),sQuery(id+"F3.wireOp",EDGE,"E9.1.1"),sQuery(id+"F3.wireOp",EDGE,"E9.1.2"),sQuery(id+"F3.wireOp",EDGE,"E9.1.3"),sQuery(id+"F3.wireOp",EDGE,"E9.1.4"),sQuery(id+"F3.wireOp",EDGE,"E9.1.5"),sQuery(id+"F3.wireOp",EDGE,"E9.2.0"),sQuery(id+"F3.wireOp",EDGE,"E9.2.1"),sQuery(id+"F3.wireOp",EDGE,"E9.2.2"),sQuery(id+"F3.wireOp",EDGE,"E9.2.3"),sQuery(id+"F3.wireOp",EDGE,"E9.2.4"),sQuery(id+"F3.wireOp",EDGE,"E9.2.5"),sQuery(id+"F3.wireOp",EDGE,"E9.3.0"),sQuery(id+"F3.wireOp",EDGE,"E9.3.1"),sQuery(id+"F3.wireOp",EDGE,"E9.3.2"),sQuery(id+"F3.wireOp",EDGE,"E9.3.3"),sQuery(id+"F3.wireOp",EDGE,"E9.3.4"),sQuery(id+"F3.wireOp",EDGE,"E9.3.5"),subQ0,sQuery(id+"F3.wireOp",EDGE,"E9.4.1"),sQuery(id+"F3.wireOp",EDGE,"E9.4.2"),sQuery(id+"F3.wireOp",EDGE,"E9.4.3"),sQuery(id+"F3.wireOp",EDGE,"E9.4.4"),sQuery(id+"F3.wireOp",EDGE,"E9.4.5"),sQuery(id+"F3.wireOp",EDGE,"E9.5.0"),sQuery(id+"F3.wireOp",EDGE,"E9.5.1"),sQuery(id+"F3.wireOp",EDGE,"E9.5.2"),sQuery(id+"F3.wireOp",EDGE,"E9.5.3"),sQuery(id+"F3.wireOp",EDGE,"E9.5.4"),sQuery(id+"F3.wireOp",EDGE,"E9.5.5"),sQuery(id+"F3.wireOp",EDGE,"E9.6.0"),sQuery(id+"F3.wireOp",EDGE,"E9.6.1"),sQuery(id+"F3.wireOp",EDGE,"E9.6.2"),sQuery(id+"F3.wireOp",EDGE,"E9.6.3"),sQuery(id+"F3.wireOp",EDGE,"E9.6.4"),sQuery(id+"F3.wireOp",EDGE,"E9.6.5"),sQuery(id+"F3.wireOp",EDGE,"E9.7.0"),sQuery(id+"F3.wireOp",EDGE,"E9.7.1"),sQuery(id+"F3.wireOp",EDGE,"E9.7.2"),sQuery(id+"F3.wireOp",EDGE,"E9.7.3"),sQuery(id+"F3.wireOp",EDGE,"E9.7.4"),sQuery(id+"F3.wireOp",EDGE,"E9.7.5")])],"isStart":false})]});}
            var Q18;
            Q18=makeQuery(id+"F4.opExtrude","CAP_EDGE",EDGE,{"disambiguationData":[OSD([sQuery(id+"F3.wireOp",EDGE,"E9.4.1")])],"isStart":false});
            var Q19;
            Q19=makeQuery(id+"F4.opExtrude","CAP_EDGE",EDGE,{"disambiguationData":[OSD([sQuery(id+"F3.wireOp",EDGE,"E9.4.2"),sQuery(id+"F3.wireOp",EDGE,"E9.4.3")])],"isStart":false});
            var Q20;
            Q20=makeQuery(id+"F4.opExtrude","CAP_EDGE",EDGE,{"disambiguationData":[OSD([sQuery(id+"F3.wireOp",EDGE,"E9.4.4")])],"isStart":false});
            var Q21;
            Q21=makeQuery(id+"F4.opExtrude","CAP_EDGE",EDGE,{"disambiguationData":[OSD([sQuery(id+"F3.wireOp",EDGE,"E9.4.5")])],"isStart":false});
            var Q22;
            {var subQ0=sQuery(id+"F3.wireOp",EDGE,"E9.4.5");var subQ1=sQuery(id+"F3.wireOp",EDGE,"E1");Q22=makeQuery(id+"F8.opFillet","BLEND_EDGE",EDGE,{"blendedFrom":[makeQuery(id+"F5.boolean.opBoolean","MERGE",EDGE,{"derivedFrom":[makeQuery(id+"F4.opExtrude","SWEPT_EDGE",EDGE,{"disambiguationData":[OSD([subQ1,subQ0])]}),makeQuery(id+"F5.opExtrude","SWEPT_EDGE",EDGE,{"disambiguationData":[OSD([subQ1,subQ0])]})]}),makeQuery(id+"F4.opExtrude","CAP_FACE",FACE,{"disambiguationData":[OSD([subQ1,sQuery(id+"F3.wireOp",EDGE,"E3"),sQuery(id+"F3.wireOp",EDGE,"E4"),sQuery(id+"F3.wireOp",EDGE,"E5"),sQuery(id+"F3.wireOp",EDGE,"E6"),sQuery(id+"F3.wireOp",EDGE,"E7"),sQuery(id+"F3.wireOp",EDGE,"E8"),sQuery(id+"F3.wireOp",EDGE,"E9.1.0"),sQuery(id+"F3.wireOp",EDGE,"E9.1.1"),sQuery(id+"F3.wireOp",EDGE,"E9.1.2"),sQuery(id+"F3.wireOp",EDGE,"E9.1.3"),sQuery(id+"F3.wireOp",EDGE,"E9.1.4"),sQuery(id+"F3.wireOp",EDGE,"E9.1.5"),sQuery(id+"F3.wireOp",EDGE,"E9.2.0"),sQuery(id+"F3.wireOp",EDGE,"E9.2.1"),sQuery(id+"F3.wireOp",EDGE,"E9.2.2"),sQuery(id+"F3.wireOp",EDGE,"E9.2.3"),sQuery(id+"F3.wireOp",EDGE,"E9.2.4"),sQuery(id+"F3.wireOp",EDGE,"E9.2.5"),sQuery(id+"F3.wireOp",EDGE,"E9.3.0"),sQuery(id+"F3.wireOp",EDGE,"E9.3.1"),sQuery(id+"F3.wireOp",EDGE,"E9.3.2"),sQuery(id+"F3.wireOp",EDGE,"E9.3.3"),sQuery(id+"F3.wireOp",EDGE,"E9.3.4"),sQuery(id+"F3.wireOp",EDGE,"E9.3.5"),sQuery(id+"F3.wireOp",EDGE,"E9.4.0"),sQuery(id+"F3.wireOp",EDGE,"E9.4.1"),sQuery(id+"F3.wireOp",EDGE,"E9.4.2"),sQuery(id+"F3.wireOp",EDGE,"E9.4.3"),sQuery(id+"F3.wireOp",EDGE,"E9.4.4"),subQ0,sQuery(id+"F3.wireOp",EDGE,"E9.5.0"),sQuery(id+"F3.wireOp",EDGE,"E9.5.1"),sQuery(id+"F3.wireOp",EDGE,"E9.5.2"),sQuery(id+"F3.wireOp",EDGE,"E9.5.3"),sQuery(id+"F3.wireOp",EDGE,"E9.5.4"),sQuery(id+"F3.wireOp",EDGE,"E9.5.5"),sQuery(id+"F3.wireOp",EDGE,"E9.6.0"),sQuery(id+"F3.wireOp",EDGE,"E9.6.1"),sQuery(id+"F3.wireOp",EDGE,"E9.6.2"),sQuery(id+"F3.wireOp",EDGE,"E9.6.3"),sQuery(id+"F3.wireOp",EDGE,"E9.6.4"),sQuery(id+"F3.wireOp",EDGE,"E9.6.5"),sQuery(id+"F3.wireOp",EDGE,"E9.7.0"),sQuery(id+"F3.wireOp",EDGE,"E9.7.1"),sQuery(id+"F3.wireOp",EDGE,"E9.7.2"),sQuery(id+"F3.wireOp",EDGE,"E9.7.3"),sQuery(id+"F3.wireOp",EDGE,"E9.7.4"),sQuery(id+"F3.wireOp",EDGE,"E9.7.5")])],"isStart":false})],"blendedInto":[makeQuery(id+"F4.opExtrude","CAP_FACE",FACE,{"disambiguationData":[OSD([subQ1,sQuery(id+"F3.wireOp",EDGE,"E3"),sQuery(id+"F3.wireOp",EDGE,"E4"),sQuery(id+"F3.wireOp",EDGE,"E5"),sQuery(id+"F3.wireOp",EDGE,"E6"),sQuery(id+"F3.wireOp",EDGE,"E7"),sQuery(id+"F3.wireOp",EDGE,"E8"),sQuery(id+"F3.wireOp",EDGE,"E9.1.0"),sQuery(id+"F3.wireOp",EDGE,"E9.1.1"),sQuery(id+"F3.wireOp",EDGE,"E9.1.2"),sQuery(id+"F3.wireOp",EDGE,"E9.1.3"),sQuery(id+"F3.wireOp",EDGE,"E9.1.4"),sQuery(id+"F3.wireOp",EDGE,"E9.1.5"),sQuery(id+"F3.wireOp",EDGE,"E9.2.0"),sQuery(id+"F3.wireOp",EDGE,"E9.2.1"),sQuery(id+"F3.wireOp",EDGE,"E9.2.2"),sQuery(id+"F3.wireOp",EDGE,"E9.2.3"),sQuery(id+"F3.wireOp",EDGE,"E9.2.4"),sQuery(id+"F3.wireOp",EDGE,"E9.2.5"),sQuery(id+"F3.wireOp",EDGE,"E9.3.0"),sQuery(id+"F3.wireOp",EDGE,"E9.3.1"),sQuery(id+"F3.wireOp",EDGE,"E9.3.2"),sQuery(id+"F3.wireOp",EDGE,"E9.3.3"),sQuery(id+"F3.wireOp",EDGE,"E9.3.4"),sQuery(id+"F3.wireOp",EDGE,"E9.3.5"),sQuery(id+"F3.wireOp",EDGE,"E9.4.0"),sQuery(id+"F3.wireOp",EDGE,"E9.4.1"),sQuery(id+"F3.wireOp",EDGE,"E9.4.2"),sQuery(id+"F3.wireOp",EDGE,"E9.4.3"),sQuery(id+"F3.wireOp",EDGE,"E9.4.4"),subQ0,sQuery(id+"F3.wireOp",EDGE,"E9.5.0"),sQuery(id+"F3.wireOp",EDGE,"E9.5.1"),sQuery(id+"F3.wireOp",EDGE,"E9.5.2"),sQuery(id+"F3.wireOp",EDGE,"E9.5.3"),sQuery(id+"F3.wireOp",EDGE,"E9.5.4"),sQuery(id+"F3.wireOp",EDGE,"E9.5.5"),sQuery(id+"F3.wireOp",EDGE,"E9.6.0"),sQuery(id+"F3.wireOp",EDGE,"E9.6.1"),sQuery(id+"F3.wireOp",EDGE,"E9.6.2"),sQuery(id+"F3.wireOp",EDGE,"E9.6.3"),sQuery(id+"F3.wireOp",EDGE,"E9.6.4"),sQuery(id+"F3.wireOp",EDGE,"E9.6.5"),sQuery(id+"F3.wireOp",EDGE,"E9.7.0"),sQuery(id+"F3.wireOp",EDGE,"E9.7.1"),sQuery(id+"F3.wireOp",EDGE,"E9.7.2"),sQuery(id+"F3.wireOp",EDGE,"E9.7.3"),sQuery(id+"F3.wireOp",EDGE,"E9.7.4"),sQuery(id+"F3.wireOp",EDGE,"E9.7.5")])],"isStart":false})]});}
            var Q23;
            Q23=makeQuery(id+"F4.opExtrude","CAP_EDGE",EDGE,{"disambiguationData":[OSD([sQuery(id+"F3.wireOp",EDGE,"E9.3.1")])],"isStart":false});
            var Q24;
            Q24=makeQuery(id+"F4.opExtrude","CAP_EDGE",EDGE,{"disambiguationData":[OSD([sQuery(id+"F3.wireOp",EDGE,"E9.3.2"),sQuery(id+"F3.wireOp",EDGE,"E9.3.3")])],"isStart":false});
            var Q25;
            Q25=makeQuery(id+"F4.opExtrude","CAP_EDGE",EDGE,{"disambiguationData":[OSD([sQuery(id+"F3.wireOp",EDGE,"E9.3.4")])],"isStart":false});
            var Q26;
            Q26=makeQuery(id+"F4.opExtrude","CAP_EDGE",EDGE,{"disambiguationData":[OSD([sQuery(id+"F3.wireOp",EDGE,"E9.3.5")])],"isStart":false});
            var Q27;
            Q27=makeQuery(id+"F4.opExtrude","CAP_EDGE",EDGE,{"disambiguationData":[OSD([sQuery(id+"F3.wireOp",EDGE,"E9.2.1")])],"isStart":false});
            var Q28;
            Q28=makeQuery(id+"F4.opExtrude","CAP_EDGE",EDGE,{"disambiguationData":[OSD([sQuery(id+"F3.wireOp",EDGE,"E9.2.2"),sQuery(id+"F3.wireOp",EDGE,"E9.2.3")])],"isStart":false});
            var Q29;
            Q29=makeQuery(id+"F4.opExtrude","CAP_EDGE",EDGE,{"disambiguationData":[OSD([sQuery(id+"F3.wireOp",EDGE,"E9.2.4")])],"isStart":false});
            var Q30;
            {var subQ0=sQuery(id+"F3.wireOp",EDGE,"E9.2.5");var subQ1=sQuery(id+"F3.wireOp",EDGE,"E1");Q30=makeQuery(id+"F8.opFillet","BLEND_EDGE",EDGE,{"blendedFrom":[makeQuery(id+"F5.boolean.opBoolean","MERGE",EDGE,{"derivedFrom":[makeQuery(id+"F4.opExtrude","SWEPT_EDGE",EDGE,{"disambiguationData":[OSD([subQ1,subQ0])]}),makeQuery(id+"F5.opExtrude","SWEPT_EDGE",EDGE,{"disambiguationData":[OSD([subQ1,subQ0])]})]}),makeQuery(id+"F5.boolean.opBoolean","MERGE",FACE,{"derivedFrom":[makeQuery(id+"F4.opExtrude","SWEPT_FACE",FACE,{"disambiguationData":[OSD([subQ0])]}),makeQuery(id+"F5.opExtrude","SWEPT_FACE",FACE,{"disambiguationData":[OSD([subQ0])]})]})],"blendedInto":[makeQuery(id+"F5.boolean.opBoolean","MERGE",FACE,{"derivedFrom":[makeQuery(id+"F4.opExtrude","SWEPT_FACE",FACE,{"disambiguationData":[OSD([subQ0])]}),makeQuery(id+"F5.opExtrude","SWEPT_FACE",FACE,{"disambiguationData":[OSD([subQ0])]})]})]});}
            var Q31;
            {var subQ0=sQuery(id+"F3.wireOp",EDGE,"E9.2.5");var subQ1=sQuery(id+"F3.wireOp",EDGE,"E1");Q31=makeQuery(id+"F8.opFillet","BLEND_EDGE",EDGE,{"blendedFrom":[makeQuery(id+"F5.boolean.opBoolean","MERGE",EDGE,{"derivedFrom":[makeQuery(id+"F4.opExtrude","SWEPT_EDGE",EDGE,{"disambiguationData":[OSD([subQ1,subQ0])]}),makeQuery(id+"F5.opExtrude","SWEPT_EDGE",EDGE,{"disambiguationData":[OSD([subQ1,subQ0])]})]}),makeQuery(id+"F4.opExtrude","CAP_FACE",FACE,{"disambiguationData":[OSD([subQ1,sQuery(id+"F3.wireOp",EDGE,"E3"),sQuery(id+"F3.wireOp",EDGE,"E4"),sQuery(id+"F3.wireOp",EDGE,"E5"),sQuery(id+"F3.wireOp",EDGE,"E6"),sQuery(id+"F3.wireOp",EDGE,"E7"),sQuery(id+"F3.wireOp",EDGE,"E8"),sQuery(id+"F3.wireOp",EDGE,"E9.1.0"),sQuery(id+"F3.wireOp",EDGE,"E9.1.1"),sQuery(id+"F3.wireOp",EDGE,"E9.1.2"),sQuery(id+"F3.wireOp",EDGE,"E9.1.3"),sQuery(id+"F3.wireOp",EDGE,"E9.1.4"),sQuery(id+"F3.wireOp",EDGE,"E9.1.5"),sQuery(id+"F3.wireOp",EDGE,"E9.2.0"),sQuery(id+"F3.wireOp",EDGE,"E9.2.1"),sQuery(id+"F3.wireOp",EDGE,"E9.2.2"),sQuery(id+"F3.wireOp",EDGE,"E9.2.3"),sQuery(id+"F3.wireOp",EDGE,"E9.2.4"),subQ0,sQuery(id+"F3.wireOp",EDGE,"E9.3.0"),sQuery(id+"F3.wireOp",EDGE,"E9.3.1"),sQuery(id+"F3.wireOp",EDGE,"E9.3.2"),sQuery(id+"F3.wireOp",EDGE,"E9.3.3"),sQuery(id+"F3.wireOp",EDGE,"E9.3.4"),sQuery(id+"F3.wireOp",EDGE,"E9.3.5"),sQuery(id+"F3.wireOp",EDGE,"E9.4.0"),sQuery(id+"F3.wireOp",EDGE,"E9.4.1"),sQuery(id+"F3.wireOp",EDGE,"E9.4.2"),sQuery(id+"F3.wireOp",EDGE,"E9.4.3"),sQuery(id+"F3.wireOp",EDGE,"E9.4.4"),sQuery(id+"F3.wireOp",EDGE,"E9.4.5"),sQuery(id+"F3.wireOp",EDGE,"E9.5.0"),sQuery(id+"F3.wireOp",EDGE,"E9.5.1"),sQuery(id+"F3.wireOp",EDGE,"E9.5.2"),sQuery(id+"F3.wireOp",EDGE,"E9.5.3"),sQuery(id+"F3.wireOp",EDGE,"E9.5.4"),sQuery(id+"F3.wireOp",EDGE,"E9.5.5"),sQuery(id+"F3.wireOp",EDGE,"E9.6.0"),sQuery(id+"F3.wireOp",EDGE,"E9.6.1"),sQuery(id+"F3.wireOp",EDGE,"E9.6.2"),sQuery(id+"F3.wireOp",EDGE,"E9.6.3"),sQuery(id+"F3.wireOp",EDGE,"E9.6.4"),sQuery(id+"F3.wireOp",EDGE,"E9.6.5"),sQuery(id+"F3.wireOp",EDGE,"E9.7.0"),sQuery(id+"F3.wireOp",EDGE,"E9.7.1"),sQuery(id+"F3.wireOp",EDGE,"E9.7.2"),sQuery(id+"F3.wireOp",EDGE,"E9.7.3"),sQuery(id+"F3.wireOp",EDGE,"E9.7.4"),sQuery(id+"F3.wireOp",EDGE,"E9.7.5")])],"isStart":false})],"blendedInto":[makeQuery(id+"F4.opExtrude","CAP_FACE",FACE,{"disambiguationData":[OSD([subQ1,sQuery(id+"F3.wireOp",EDGE,"E3"),sQuery(id+"F3.wireOp",EDGE,"E4"),sQuery(id+"F3.wireOp",EDGE,"E5"),sQuery(id+"F3.wireOp",EDGE,"E6"),sQuery(id+"F3.wireOp",EDGE,"E7"),sQuery(id+"F3.wireOp",EDGE,"E8"),sQuery(id+"F3.wireOp",EDGE,"E9.1.0"),sQuery(id+"F3.wireOp",EDGE,"E9.1.1"),sQuery(id+"F3.wireOp",EDGE,"E9.1.2"),sQuery(id+"F3.wireOp",EDGE,"E9.1.3"),sQuery(id+"F3.wireOp",EDGE,"E9.1.4"),sQuery(id+"F3.wireOp",EDGE,"E9.1.5"),sQuery(id+"F3.wireOp",EDGE,"E9.2.0"),sQuery(id+"F3.wireOp",EDGE,"E9.2.1"),sQuery(id+"F3.wireOp",EDGE,"E9.2.2"),sQuery(id+"F3.wireOp",EDGE,"E9.2.3"),sQuery(id+"F3.wireOp",EDGE,"E9.2.4"),subQ0,sQuery(id+"F3.wireOp",EDGE,"E9.3.0"),sQuery(id+"F3.wireOp",EDGE,"E9.3.1"),sQuery(id+"F3.wireOp",EDGE,"E9.3.2"),sQuery(id+"F3.wireOp",EDGE,"E9.3.3"),sQuery(id+"F3.wireOp",EDGE,"E9.3.4"),sQuery(id+"F3.wireOp",EDGE,"E9.3.5"),sQuery(id+"F3.wireOp",EDGE,"E9.4.0"),sQuery(id+"F3.wireOp",EDGE,"E9.4.1"),sQuery(id+"F3.wireOp",EDGE,"E9.4.2"),sQuery(id+"F3.wireOp",EDGE,"E9.4.3"),sQuery(id+"F3.wireOp",EDGE,"E9.4.4"),sQuery(id+"F3.wireOp",EDGE,"E9.4.5"),sQuery(id+"F3.wireOp",EDGE,"E9.5.0"),sQuery(id+"F3.wireOp",EDGE,"E9.5.1"),sQuery(id+"F3.wireOp",EDGE,"E9.5.2"),sQuery(id+"F3.wireOp",EDGE,"E9.5.3"),sQuery(id+"F3.wireOp",EDGE,"E9.5.4"),sQuery(id+"F3.wireOp",EDGE,"E9.5.5"),sQuery(id+"F3.wireOp",EDGE,"E9.6.0"),sQuery(id+"F3.wireOp",EDGE,"E9.6.1"),sQuery(id+"F3.wireOp",EDGE,"E9.6.2"),sQuery(id+"F3.wireOp",EDGE,"E9.6.3"),sQuery(id+"F3.wireOp",EDGE,"E9.6.4"),sQuery(id+"F3.wireOp",EDGE,"E9.6.5"),sQuery(id+"F3.wireOp",EDGE,"E9.7.0"),sQuery(id+"F3.wireOp",EDGE,"E9.7.1"),sQuery(id+"F3.wireOp",EDGE,"E9.7.2"),sQuery(id+"F3.wireOp",EDGE,"E9.7.3"),sQuery(id+"F3.wireOp",EDGE,"E9.7.4"),sQuery(id+"F3.wireOp",EDGE,"E9.7.5")])],"isStart":false})]});}
            var Q32;
            {var subQ0=sQuery(id+"F3.wireOp",EDGE,"E1");var subQ1=makeQuery(id+"F3.imprint","INTERSECT",VERTEX,{"derivedFrom":[subQ0,sQuery(id+"F3.wireOp",EDGE,"E9.2.4")]});var subQ2=makeQuery(id+"F3.imprint","INTERSECT",VERTEX,{"derivedFrom":[subQ0,sQuery(id+"F3.wireOp",EDGE,"E9.1.1")]});Q32=makeQuery(id+"F4.opExtrude","CAP_EDGE",EDGE,{"disambiguationData":[OSD([subQ0]),TDD([makeQuery(id+"F3.imprint","IMPRINT",EDGE,{"disambiguationData":[TD([[makeQuery(id+"F3.imprint","INTERSECT",VERTEX,{"derivedFrom":[subQ0,sQuery(id+"F3.wireOp",EDGE,"E9.1.0")]}),-1.0]])],"derivedFrom":subQ0}),makeQuery(id+"F3.imprint","IMPRINT",EDGE,{"disambiguationData":[TD([[subQ2,-1.0]])],"derivedFrom":subQ0}),makeQuery(id+"F3.imprint","IMPRINT",EDGE,{"disambiguationData":[TD([[subQ1,-1.0]])],"derivedFrom":subQ0})])],"isStart":false});}
            var Q33;
            Q33=makeQuery(id+"F4.opExtrude","CAP_EDGE",EDGE,{"disambiguationData":[OSD([sQuery(id+"F3.wireOp",EDGE,"E9.2.5")])],"isStart":false});
            var Q34;
            Q34=makeQuery(id+"F4.opExtrude","CAP_EDGE",EDGE,{"disambiguationData":[OSD([sQuery(id+"F3.wireOp",EDGE,"E9.1.1")])],"isStart":false});
            var Q35;
            Q35=makeQuery(id+"F4.opExtrude","CAP_EDGE",EDGE,{"disambiguationData":[OSD([sQuery(id+"F3.wireOp",EDGE,"E9.1.2"),sQuery(id+"F3.wireOp",EDGE,"E9.1.3")])],"isStart":false});
            var Q36;
            Q36=makeQuery(id+"F4.opExtrude","CAP_EDGE",EDGE,{"disambiguationData":[OSD([sQuery(id+"F3.wireOp",EDGE,"E9.1.4")])],"isStart":false});
            var Q37;
            Q37=makeQuery(id+"F4.opExtrude","CAP_EDGE",EDGE,{"disambiguationData":[OSD([sQuery(id+"F3.wireOp",EDGE,"E9.1.5")])],"isStart":false});
            var Q38;
            {var subQ0=sQuery(id+"F3.wireOp",EDGE,"E9.1.5");var subQ1=sQuery(id+"F3.wireOp",EDGE,"E1");Q38=makeQuery(id+"F8.opFillet","BLEND_EDGE",EDGE,{"blendedFrom":[makeQuery(id+"F5.boolean.opBoolean","MERGE",EDGE,{"derivedFrom":[makeQuery(id+"F4.opExtrude","SWEPT_EDGE",EDGE,{"disambiguationData":[OSD([subQ1,subQ0])]}),makeQuery(id+"F5.opExtrude","SWEPT_EDGE",EDGE,{"disambiguationData":[OSD([subQ1,subQ0])]})]}),makeQuery(id+"F4.opExtrude","CAP_FACE",FACE,{"disambiguationData":[OSD([subQ1,sQuery(id+"F3.wireOp",EDGE,"E3"),sQuery(id+"F3.wireOp",EDGE,"E4"),sQuery(id+"F3.wireOp",EDGE,"E5"),sQuery(id+"F3.wireOp",EDGE,"E6"),sQuery(id+"F3.wireOp",EDGE,"E7"),sQuery(id+"F3.wireOp",EDGE,"E8"),sQuery(id+"F3.wireOp",EDGE,"E9.1.0"),sQuery(id+"F3.wireOp",EDGE,"E9.1.1"),sQuery(id+"F3.wireOp",EDGE,"E9.1.2"),sQuery(id+"F3.wireOp",EDGE,"E9.1.3"),sQuery(id+"F3.wireOp",EDGE,"E9.1.4"),subQ0,sQuery(id+"F3.wireOp",EDGE,"E9.2.0"),sQuery(id+"F3.wireOp",EDGE,"E9.2.1"),sQuery(id+"F3.wireOp",EDGE,"E9.2.2"),sQuery(id+"F3.wireOp",EDGE,"E9.2.3"),sQuery(id+"F3.wireOp",EDGE,"E9.2.4"),sQuery(id+"F3.wireOp",EDGE,"E9.2.5"),sQuery(id+"F3.wireOp",EDGE,"E9.3.0"),sQuery(id+"F3.wireOp",EDGE,"E9.3.1"),sQuery(id+"F3.wireOp",EDGE,"E9.3.2"),sQuery(id+"F3.wireOp",EDGE,"E9.3.3"),sQuery(id+"F3.wireOp",EDGE,"E9.3.4"),sQuery(id+"F3.wireOp",EDGE,"E9.3.5"),sQuery(id+"F3.wireOp",EDGE,"E9.4.0"),sQuery(id+"F3.wireOp",EDGE,"E9.4.1"),sQuery(id+"F3.wireOp",EDGE,"E9.4.2"),sQuery(id+"F3.wireOp",EDGE,"E9.4.3"),sQuery(id+"F3.wireOp",EDGE,"E9.4.4"),sQuery(id+"F3.wireOp",EDGE,"E9.4.5"),sQuery(id+"F3.wireOp",EDGE,"E9.5.0"),sQuery(id+"F3.wireOp",EDGE,"E9.5.1"),sQuery(id+"F3.wireOp",EDGE,"E9.5.2"),sQuery(id+"F3.wireOp",EDGE,"E9.5.3"),sQuery(id+"F3.wireOp",EDGE,"E9.5.4"),sQuery(id+"F3.wireOp",EDGE,"E9.5.5"),sQuery(id+"F3.wireOp",EDGE,"E9.6.0"),sQuery(id+"F3.wireOp",EDGE,"E9.6.1"),sQuery(id+"F3.wireOp",EDGE,"E9.6.2"),sQuery(id+"F3.wireOp",EDGE,"E9.6.3"),sQuery(id+"F3.wireOp",EDGE,"E9.6.4"),sQuery(id+"F3.wireOp",EDGE,"E9.6.5"),sQuery(id+"F3.wireOp",EDGE,"E9.7.0"),sQuery(id+"F3.wireOp",EDGE,"E9.7.1"),sQuery(id+"F3.wireOp",EDGE,"E9.7.2"),sQuery(id+"F3.wireOp",EDGE,"E9.7.3"),sQuery(id+"F3.wireOp",EDGE,"E9.7.4"),sQuery(id+"F3.wireOp",EDGE,"E9.7.5")])],"isStart":false})],"blendedInto":[makeQuery(id+"F4.opExtrude","CAP_FACE",FACE,{"disambiguationData":[OSD([subQ1,sQuery(id+"F3.wireOp",EDGE,"E3"),sQuery(id+"F3.wireOp",EDGE,"E4"),sQuery(id+"F3.wireOp",EDGE,"E5"),sQuery(id+"F3.wireOp",EDGE,"E6"),sQuery(id+"F3.wireOp",EDGE,"E7"),sQuery(id+"F3.wireOp",EDGE,"E8"),sQuery(id+"F3.wireOp",EDGE,"E9.1.0"),sQuery(id+"F3.wireOp",EDGE,"E9.1.1"),sQuery(id+"F3.wireOp",EDGE,"E9.1.2"),sQuery(id+"F3.wireOp",EDGE,"E9.1.3"),sQuery(id+"F3.wireOp",EDGE,"E9.1.4"),subQ0,sQuery(id+"F3.wireOp",EDGE,"E9.2.0"),sQuery(id+"F3.wireOp",EDGE,"E9.2.1"),sQuery(id+"F3.wireOp",EDGE,"E9.2.2"),sQuery(id+"F3.wireOp",EDGE,"E9.2.3"),sQuery(id+"F3.wireOp",EDGE,"E9.2.4"),sQuery(id+"F3.wireOp",EDGE,"E9.2.5"),sQuery(id+"F3.wireOp",EDGE,"E9.3.0"),sQuery(id+"F3.wireOp",EDGE,"E9.3.1"),sQuery(id+"F3.wireOp",EDGE,"E9.3.2"),sQuery(id+"F3.wireOp",EDGE,"E9.3.3"),sQuery(id+"F3.wireOp",EDGE,"E9.3.4"),sQuery(id+"F3.wireOp",EDGE,"E9.3.5"),sQuery(id+"F3.wireOp",EDGE,"E9.4.0"),sQuery(id+"F3.wireOp",EDGE,"E9.4.1"),sQuery(id+"F3.wireOp",EDGE,"E9.4.2"),sQuery(id+"F3.wireOp",EDGE,"E9.4.3"),sQuery(id+"F3.wireOp",EDGE,"E9.4.4"),sQuery(id+"F3.wireOp",EDGE,"E9.4.5"),sQuery(id+"F3.wireOp",EDGE,"E9.5.0"),sQuery(id+"F3.wireOp",EDGE,"E9.5.1"),sQuery(id+"F3.wireOp",EDGE,"E9.5.2"),sQuery(id+"F3.wireOp",EDGE,"E9.5.3"),sQuery(id+"F3.wireOp",EDGE,"E9.5.4"),sQuery(id+"F3.wireOp",EDGE,"E9.5.5"),sQuery(id+"F3.wireOp",EDGE,"E9.6.0"),sQuery(id+"F3.wireOp",EDGE,"E9.6.1"),sQuery(id+"F3.wireOp",EDGE,"E9.6.2"),sQuery(id+"F3.wireOp",EDGE,"E9.6.3"),sQuery(id+"F3.wireOp",EDGE,"E9.6.4"),sQuery(id+"F3.wireOp",EDGE,"E9.6.5"),sQuery(id+"F3.wireOp",EDGE,"E9.7.0"),sQuery(id+"F3.wireOp",EDGE,"E9.7.1"),sQuery(id+"F3.wireOp",EDGE,"E9.7.2"),sQuery(id+"F3.wireOp",EDGE,"E9.7.3"),sQuery(id+"F3.wireOp",EDGE,"E9.7.4"),sQuery(id+"F3.wireOp",EDGE,"E9.7.5")])],"isStart":false})]});}
            var Q39;
            {var subQ0=sQuery(id+"F3.wireOp",EDGE,"E1");var subQ1=makeQuery(id+"F3.imprint","INTERSECT",VERTEX,{"derivedFrom":[subQ0,sQuery(id+"F3.wireOp",EDGE,"E9.1.4")]});var subQ2=makeQuery(id+"F3.imprint","INTERSECT",VERTEX,{"derivedFrom":[subQ0,sQuery(id+"F3.wireOp",EDGE,"E6")]});Q39=makeQuery(id+"F4.opExtrude","CAP_EDGE",EDGE,{"disambiguationData":[OSD([subQ0]),TDD([makeQuery(id+"F3.imprint","IMPRINT",EDGE,{"disambiguationData":[TD([[subQ2,1.0]])],"derivedFrom":subQ0}),makeQuery(id+"F3.imprint","IMPRINT",EDGE,{"disambiguationData":[TD([[subQ2,-1.0]])],"derivedFrom":subQ0}),makeQuery(id+"F3.imprint","IMPRINT",EDGE,{"disambiguationData":[TD([[subQ1,-1.0]])],"derivedFrom":subQ0})])],"isStart":false});}
            var Q40;
            Q40=makeQuery(id+"F4.opExtrude","CAP_EDGE",EDGE,{"disambiguationData":[OSD([sQuery(id+"F3.wireOp",EDGE,"E6")])],"isStart":false});
            var Q41;
            Q41=makeQuery(id+"F4.opExtrude","CAP_EDGE",EDGE,{"disambiguationData":[OSD([sQuery(id+"F3.wireOp",EDGE,"E3"),sQuery(id+"F3.wireOp",EDGE,"E5")])],"isStart":false});
            var Q42;
            Q42=makeQuery(id+"F4.opExtrude","CAP_EDGE",EDGE,{"disambiguationData":[OSD([sQuery(id+"F3.wireOp",EDGE,"E4")])],"isStart":false});
            var Q43;
            Q43=makeQuery(id+"F4.opExtrude","CAP_EDGE",EDGE,{"disambiguationData":[OSD([sQuery(id+"F3.wireOp",EDGE,"E7")])],"isStart":false});
            var Q44;
            Q44=makeQuery(id+"F4.opExtrude","CAP_EDGE",EDGE,{"disambiguationData":[OSD([sQuery(id+"F3.wireOp",EDGE,"E9.7.1")])],"isStart":false});
            var Q45;
            Q45=makeQuery(id+"F4.opExtrude","CAP_EDGE",EDGE,{"disambiguationData":[OSD([sQuery(id+"F3.wireOp",EDGE,"E9.7.2"),sQuery(id+"F3.wireOp",EDGE,"E9.7.3")])],"isStart":false});
            var Q46;
            Q46=makeQuery(id+"F4.opExtrude","CAP_EDGE",EDGE,{"disambiguationData":[OSD([sQuery(id+"F3.wireOp",EDGE,"E9.7.4")])],"isStart":false});
            fillet(context, id + "F9", {"entities" : qUnion([Q0, Q1, Q2, Q3, Q4, Q5, Q6, Q7, Q8, Q9, Q10, Q11, Q12, Q13, Q14, Q15, Q16, Q17, Q18, Q19, Q20, Q21, Q22, Q23, Q24, Q25, Q26, Q27, Q28, Q29, Q30, Q31, Q32, Q33, Q34, Q35, Q36, Q37, Q38, Q39, Q40, Q41, Q42, Q43, Q44, Q45, Q46]), "radius" : 0.1 * mm, "tangentPropagation" : true, "allowEdgeOverflow" : false});
        }
        {
            var Q0;
            {var subQ0=sQuery(id+"F3.wireOp",EDGE,"E1");var subQ1=makeQuery(id+"F3.imprint","INTERSECT",VERTEX,{"derivedFrom":[subQ0,sQuery(id+"F3.wireOp",EDGE,"E9.3.4")]});var subQ2=makeQuery(id+"F3.imprint","INTERSECT",VERTEX,{"derivedFrom":[subQ0,sQuery(id+"F3.wireOp",EDGE,"E9.2.1")]});Q0=makeQuery(id+"F5.opExtrude","CAP_EDGE",EDGE,{"disambiguationData":[OSD([subQ0]),TDD([makeQuery(id+"F4.opExtrude","CAP_EDGE",EDGE,{"disambiguationData":[OSD([subQ0]),TDD([makeQuery(id+"F3.imprint","IMPRINT",EDGE,{"disambiguationData":[TD([[makeQuery(id+"F3.imprint","INTERSECT",VERTEX,{"derivedFrom":[subQ0,sQuery(id+"F3.wireOp",EDGE,"E9.2.0")]}),-1.0]])],"derivedFrom":subQ0}),makeQuery(id+"F3.imprint","IMPRINT",EDGE,{"disambiguationData":[TD([[subQ2,-1.0]])],"derivedFrom":subQ0}),makeQuery(id+"F3.imprint","IMPRINT",EDGE,{"disambiguationData":[TD([[subQ1,-1.0]])],"derivedFrom":subQ0})])],"isStart":true})])],"isStart":false});}
            var Q1;
            {var subQ0=sQuery(id+"F3.wireOp",EDGE,"E9.3.5");var subQ1=sQuery(id+"F3.wireOp",EDGE,"E1");Q1=makeQuery(id+"F8.opFillet","BLEND_EDGE",EDGE,{"blendedFrom":[makeQuery(id+"F5.boolean.opBoolean","MERGE",EDGE,{"derivedFrom":[makeQuery(id+"F4.opExtrude","SWEPT_EDGE",EDGE,{"disambiguationData":[OSD([subQ1,subQ0])]}),makeQuery(id+"F5.opExtrude","SWEPT_EDGE",EDGE,{"disambiguationData":[OSD([subQ1,subQ0])]})]}),makeQuery(id+"F5.opExtrude","CAP_FACE",FACE,{"disambiguationData":[OSD([subQ1,sQuery(id+"F3.wireOp",EDGE,"E3"),sQuery(id+"F3.wireOp",EDGE,"E4"),sQuery(id+"F3.wireOp",EDGE,"E5"),sQuery(id+"F3.wireOp",EDGE,"E6"),sQuery(id+"F3.wireOp",EDGE,"E7"),sQuery(id+"F3.wireOp",EDGE,"E8"),sQuery(id+"F3.wireOp",EDGE,"E9.1.0"),sQuery(id+"F3.wireOp",EDGE,"E9.1.1"),sQuery(id+"F3.wireOp",EDGE,"E9.1.2"),sQuery(id+"F3.wireOp",EDGE,"E9.1.3"),sQuery(id+"F3.wireOp",EDGE,"E9.1.4"),sQuery(id+"F3.wireOp",EDGE,"E9.1.5"),sQuery(id+"F3.wireOp",EDGE,"E9.2.0"),sQuery(id+"F3.wireOp",EDGE,"E9.2.1"),sQuery(id+"F3.wireOp",EDGE,"E9.2.2"),sQuery(id+"F3.wireOp",EDGE,"E9.2.3"),sQuery(id+"F3.wireOp",EDGE,"E9.2.4"),sQuery(id+"F3.wireOp",EDGE,"E9.2.5"),sQuery(id+"F3.wireOp",EDGE,"E9.3.0"),sQuery(id+"F3.wireOp",EDGE,"E9.3.1"),sQuery(id+"F3.wireOp",EDGE,"E9.3.2"),sQuery(id+"F3.wireOp",EDGE,"E9.3.3"),sQuery(id+"F3.wireOp",EDGE,"E9.3.4"),subQ0,sQuery(id+"F3.wireOp",EDGE,"E9.4.0"),sQuery(id+"F3.wireOp",EDGE,"E9.4.1"),sQuery(id+"F3.wireOp",EDGE,"E9.4.2"),sQuery(id+"F3.wireOp",EDGE,"E9.4.3"),sQuery(id+"F3.wireOp",EDGE,"E9.4.4"),sQuery(id+"F3.wireOp",EDGE,"E9.4.5"),sQuery(id+"F3.wireOp",EDGE,"E9.5.0"),sQuery(id+"F3.wireOp",EDGE,"E9.5.1"),sQuery(id+"F3.wireOp",EDGE,"E9.5.2"),sQuery(id+"F3.wireOp",EDGE,"E9.5.3"),sQuery(id+"F3.wireOp",EDGE,"E9.5.4"),sQuery(id+"F3.wireOp",EDGE,"E9.5.5"),sQuery(id+"F3.wireOp",EDGE,"E9.6.0"),sQuery(id+"F3.wireOp",EDGE,"E9.6.1"),sQuery(id+"F3.wireOp",EDGE,"E9.6.2"),sQuery(id+"F3.wireOp",EDGE,"E9.6.3"),sQuery(id+"F3.wireOp",EDGE,"E9.6.4"),sQuery(id+"F3.wireOp",EDGE,"E9.6.5"),sQuery(id+"F3.wireOp",EDGE,"E9.7.0"),sQuery(id+"F3.wireOp",EDGE,"E9.7.1"),sQuery(id+"F3.wireOp",EDGE,"E9.7.2"),sQuery(id+"F3.wireOp",EDGE,"E9.7.3"),sQuery(id+"F3.wireOp",EDGE,"E9.7.4"),sQuery(id+"F3.wireOp",EDGE,"E9.7.5")])],"isStart":false})],"blendedInto":[makeQuery(id+"F5.opExtrude","CAP_FACE",FACE,{"disambiguationData":[OSD([subQ1,sQuery(id+"F3.wireOp",EDGE,"E3"),sQuery(id+"F3.wireOp",EDGE,"E4"),sQuery(id+"F3.wireOp",EDGE,"E5"),sQuery(id+"F3.wireOp",EDGE,"E6"),sQuery(id+"F3.wireOp",EDGE,"E7"),sQuery(id+"F3.wireOp",EDGE,"E8"),sQuery(id+"F3.wireOp",EDGE,"E9.1.0"),sQuery(id+"F3.wireOp",EDGE,"E9.1.1"),sQuery(id+"F3.wireOp",EDGE,"E9.1.2"),sQuery(id+"F3.wireOp",EDGE,"E9.1.3"),sQuery(id+"F3.wireOp",EDGE,"E9.1.4"),sQuery(id+"F3.wireOp",EDGE,"E9.1.5"),sQuery(id+"F3.wireOp",EDGE,"E9.2.0"),sQuery(id+"F3.wireOp",EDGE,"E9.2.1"),sQuery(id+"F3.wireOp",EDGE,"E9.2.2"),sQuery(id+"F3.wireOp",EDGE,"E9.2.3"),sQuery(id+"F3.wireOp",EDGE,"E9.2.4"),sQuery(id+"F3.wireOp",EDGE,"E9.2.5"),sQuery(id+"F3.wireOp",EDGE,"E9.3.0"),sQuery(id+"F3.wireOp",EDGE,"E9.3.1"),sQuery(id+"F3.wireOp",EDGE,"E9.3.2"),sQuery(id+"F3.wireOp",EDGE,"E9.3.3"),sQuery(id+"F3.wireOp",EDGE,"E9.3.4"),subQ0,sQuery(id+"F3.wireOp",EDGE,"E9.4.0"),sQuery(id+"F3.wireOp",EDGE,"E9.4.1"),sQuery(id+"F3.wireOp",EDGE,"E9.4.2"),sQuery(id+"F3.wireOp",EDGE,"E9.4.3"),sQuery(id+"F3.wireOp",EDGE,"E9.4.4"),sQuery(id+"F3.wireOp",EDGE,"E9.4.5"),sQuery(id+"F3.wireOp",EDGE,"E9.5.0"),sQuery(id+"F3.wireOp",EDGE,"E9.5.1"),sQuery(id+"F3.wireOp",EDGE,"E9.5.2"),sQuery(id+"F3.wireOp",EDGE,"E9.5.3"),sQuery(id+"F3.wireOp",EDGE,"E9.5.4"),sQuery(id+"F3.wireOp",EDGE,"E9.5.5"),sQuery(id+"F3.wireOp",EDGE,"E9.6.0"),sQuery(id+"F3.wireOp",EDGE,"E9.6.1"),sQuery(id+"F3.wireOp",EDGE,"E9.6.2"),sQuery(id+"F3.wireOp",EDGE,"E9.6.3"),sQuery(id+"F3.wireOp",EDGE,"E9.6.4"),sQuery(id+"F3.wireOp",EDGE,"E9.6.5"),sQuery(id+"F3.wireOp",EDGE,"E9.7.0"),sQuery(id+"F3.wireOp",EDGE,"E9.7.1"),sQuery(id+"F3.wireOp",EDGE,"E9.7.2"),sQuery(id+"F3.wireOp",EDGE,"E9.7.3"),sQuery(id+"F3.wireOp",EDGE,"E9.7.4"),sQuery(id+"F3.wireOp",EDGE,"E9.7.5")])],"isStart":false})]});}
            var Q2;
            Q2=makeQuery(id+"F5.opExtrude","CAP_EDGE",EDGE,{"disambiguationData":[OSD([sQuery(id+"F3.wireOp",EDGE,"E9.3.5")])],"isStart":false});
            var Q3;
            Q3=makeQuery(id+"F5.opExtrude","CAP_EDGE",EDGE,{"disambiguationData":[OSD([sQuery(id+"F3.wireOp",EDGE,"E9.3.2"),sQuery(id+"F3.wireOp",EDGE,"E9.3.3")])],"isStart":false});
            var Q4;
            Q4=makeQuery(id+"F5.opExtrude","CAP_EDGE",EDGE,{"disambiguationData":[OSD([sQuery(id+"F3.wireOp",EDGE,"E9.3.4")])],"isStart":false});
            var Q5;
            Q5=makeQuery(id+"F5.opExtrude","CAP_EDGE",EDGE,{"disambiguationData":[OSD([sQuery(id+"F3.wireOp",EDGE,"E9.3.1")])],"isStart":false});
            var Q6;
            Q6=makeQuery(id+"F5.opExtrude","CAP_EDGE",EDGE,{"disambiguationData":[OSD([sQuery(id+"F3.wireOp",EDGE,"E9.3.0")])],"isStart":false});
            var Q7;
            {var subQ0=sQuery(id+"F3.wireOp",EDGE,"E9.3.0");var subQ1=sQuery(id+"F3.wireOp",EDGE,"E1");Q7=makeQuery(id+"F8.opFillet","BLEND_EDGE",EDGE,{"blendedFrom":[makeQuery(id+"F5.boolean.opBoolean","MERGE",EDGE,{"derivedFrom":[makeQuery(id+"F4.opExtrude","SWEPT_EDGE",EDGE,{"disambiguationData":[OSD([subQ1,subQ0])]}),makeQuery(id+"F5.opExtrude","SWEPT_EDGE",EDGE,{"disambiguationData":[OSD([subQ1,subQ0])]})]}),makeQuery(id+"F5.opExtrude","CAP_FACE",FACE,{"disambiguationData":[OSD([subQ1,sQuery(id+"F3.wireOp",EDGE,"E3"),sQuery(id+"F3.wireOp",EDGE,"E4"),sQuery(id+"F3.wireOp",EDGE,"E5"),sQuery(id+"F3.wireOp",EDGE,"E6"),sQuery(id+"F3.wireOp",EDGE,"E7"),sQuery(id+"F3.wireOp",EDGE,"E8"),sQuery(id+"F3.wireOp",EDGE,"E9.1.0"),sQuery(id+"F3.wireOp",EDGE,"E9.1.1"),sQuery(id+"F3.wireOp",EDGE,"E9.1.2"),sQuery(id+"F3.wireOp",EDGE,"E9.1.3"),sQuery(id+"F3.wireOp",EDGE,"E9.1.4"),sQuery(id+"F3.wireOp",EDGE,"E9.1.5"),sQuery(id+"F3.wireOp",EDGE,"E9.2.0"),sQuery(id+"F3.wireOp",EDGE,"E9.2.1"),sQuery(id+"F3.wireOp",EDGE,"E9.2.2"),sQuery(id+"F3.wireOp",EDGE,"E9.2.3"),sQuery(id+"F3.wireOp",EDGE,"E9.2.4"),sQuery(id+"F3.wireOp",EDGE,"E9.2.5"),subQ0,sQuery(id+"F3.wireOp",EDGE,"E9.3.1"),sQuery(id+"F3.wireOp",EDGE,"E9.3.2"),sQuery(id+"F3.wireOp",EDGE,"E9.3.3"),sQuery(id+"F3.wireOp",EDGE,"E9.3.4"),sQuery(id+"F3.wireOp",EDGE,"E9.3.5"),sQuery(id+"F3.wireOp",EDGE,"E9.4.0"),sQuery(id+"F3.wireOp",EDGE,"E9.4.1"),sQuery(id+"F3.wireOp",EDGE,"E9.4.2"),sQuery(id+"F3.wireOp",EDGE,"E9.4.3"),sQuery(id+"F3.wireOp",EDGE,"E9.4.4"),sQuery(id+"F3.wireOp",EDGE,"E9.4.5"),sQuery(id+"F3.wireOp",EDGE,"E9.5.0"),sQuery(id+"F3.wireOp",EDGE,"E9.5.1"),sQuery(id+"F3.wireOp",EDGE,"E9.5.2"),sQuery(id+"F3.wireOp",EDGE,"E9.5.3"),sQuery(id+"F3.wireOp",EDGE,"E9.5.4"),sQuery(id+"F3.wireOp",EDGE,"E9.5.5"),sQuery(id+"F3.wireOp",EDGE,"E9.6.0"),sQuery(id+"F3.wireOp",EDGE,"E9.6.1"),sQuery(id+"F3.wireOp",EDGE,"E9.6.2"),sQuery(id+"F3.wireOp",EDGE,"E9.6.3"),sQuery(id+"F3.wireOp",EDGE,"E9.6.4"),sQuery(id+"F3.wireOp",EDGE,"E9.6.5"),sQuery(id+"F3.wireOp",EDGE,"E9.7.0"),sQuery(id+"F3.wireOp",EDGE,"E9.7.1"),sQuery(id+"F3.wireOp",EDGE,"E9.7.2"),sQuery(id+"F3.wireOp",EDGE,"E9.7.3"),sQuery(id+"F3.wireOp",EDGE,"E9.7.4"),sQuery(id+"F3.wireOp",EDGE,"E9.7.5")])],"isStart":false})],"blendedInto":[makeQuery(id+"F5.opExtrude","CAP_FACE",FACE,{"disambiguationData":[OSD([subQ1,sQuery(id+"F3.wireOp",EDGE,"E3"),sQuery(id+"F3.wireOp",EDGE,"E4"),sQuery(id+"F3.wireOp",EDGE,"E5"),sQuery(id+"F3.wireOp",EDGE,"E6"),sQuery(id+"F3.wireOp",EDGE,"E7"),sQuery(id+"F3.wireOp",EDGE,"E8"),sQuery(id+"F3.wireOp",EDGE,"E9.1.0"),sQuery(id+"F3.wireOp",EDGE,"E9.1.1"),sQuery(id+"F3.wireOp",EDGE,"E9.1.2"),sQuery(id+"F3.wireOp",EDGE,"E9.1.3"),sQuery(id+"F3.wireOp",EDGE,"E9.1.4"),sQuery(id+"F3.wireOp",EDGE,"E9.1.5"),sQuery(id+"F3.wireOp",EDGE,"E9.2.0"),sQuery(id+"F3.wireOp",EDGE,"E9.2.1"),sQuery(id+"F3.wireOp",EDGE,"E9.2.2"),sQuery(id+"F3.wireOp",EDGE,"E9.2.3"),sQuery(id+"F3.wireOp",EDGE,"E9.2.4"),sQuery(id+"F3.wireOp",EDGE,"E9.2.5"),subQ0,sQuery(id+"F3.wireOp",EDGE,"E9.3.1"),sQuery(id+"F3.wireOp",EDGE,"E9.3.2"),sQuery(id+"F3.wireOp",EDGE,"E9.3.3"),sQuery(id+"F3.wireOp",EDGE,"E9.3.4"),sQuery(id+"F3.wireOp",EDGE,"E9.3.5"),sQuery(id+"F3.wireOp",EDGE,"E9.4.0"),sQuery(id+"F3.wireOp",EDGE,"E9.4.1"),sQuery(id+"F3.wireOp",EDGE,"E9.4.2"),sQuery(id+"F3.wireOp",EDGE,"E9.4.3"),sQuery(id+"F3.wireOp",EDGE,"E9.4.4"),sQuery(id+"F3.wireOp",EDGE,"E9.4.5"),sQuery(id+"F3.wireOp",EDGE,"E9.5.0"),sQuery(id+"F3.wireOp",EDGE,"E9.5.1"),sQuery(id+"F3.wireOp",EDGE,"E9.5.2"),sQuery(id+"F3.wireOp",EDGE,"E9.5.3"),sQuery(id+"F3.wireOp",EDGE,"E9.5.4"),sQuery(id+"F3.wireOp",EDGE,"E9.5.5"),sQuery(id+"F3.wireOp",EDGE,"E9.6.0"),sQuery(id+"F3.wireOp",EDGE,"E9.6.1"),sQuery(id+"F3.wireOp",EDGE,"E9.6.2"),sQuery(id+"F3.wireOp",EDGE,"E9.6.3"),sQuery(id+"F3.wireOp",EDGE,"E9.6.4"),sQuery(id+"F3.wireOp",EDGE,"E9.6.5"),sQuery(id+"F3.wireOp",EDGE,"E9.7.0"),sQuery(id+"F3.wireOp",EDGE,"E9.7.1"),sQuery(id+"F3.wireOp",EDGE,"E9.7.2"),sQuery(id+"F3.wireOp",EDGE,"E9.7.3"),sQuery(id+"F3.wireOp",EDGE,"E9.7.4"),sQuery(id+"F3.wireOp",EDGE,"E9.7.5")])],"isStart":false})]});}
            var Q8;
            {var subQ0=sQuery(id+"F3.wireOp",EDGE,"E1");var subQ1=makeQuery(id+"F3.imprint","INTERSECT",VERTEX,{"derivedFrom":[subQ0,sQuery(id+"F3.wireOp",EDGE,"E9.4.4")]});var subQ2=makeQuery(id+"F3.imprint","INTERSECT",VERTEX,{"derivedFrom":[subQ0,sQuery(id+"F3.wireOp",EDGE,"E9.3.1")]});Q8=makeQuery(id+"F5.opExtrude","CAP_EDGE",EDGE,{"disambiguationData":[OSD([subQ0]),TDD([makeQuery(id+"F4.opExtrude","CAP_EDGE",EDGE,{"disambiguationData":[OSD([subQ0]),TDD([makeQuery(id+"F3.imprint","IMPRINT",EDGE,{"disambiguationData":[TD([[makeQuery(id+"F3.imprint","INTERSECT",VERTEX,{"derivedFrom":[subQ0,sQuery(id+"F3.wireOp",EDGE,"E9.3.0")]}),-1.0]])],"derivedFrom":subQ0}),makeQuery(id+"F3.imprint","IMPRINT",EDGE,{"disambiguationData":[TD([[subQ2,-1.0]])],"derivedFrom":subQ0}),makeQuery(id+"F3.imprint","IMPRINT",EDGE,{"disambiguationData":[TD([[subQ1,-1.0]])],"derivedFrom":subQ0})])],"isStart":true})])],"isStart":false});}
            var Q9;
            {var subQ0=sQuery(id+"F3.wireOp",EDGE,"E9.4.5");var subQ1=sQuery(id+"F3.wireOp",EDGE,"E1");Q9=makeQuery(id+"F8.opFillet","BLEND_EDGE",EDGE,{"blendedFrom":[makeQuery(id+"F5.boolean.opBoolean","MERGE",EDGE,{"derivedFrom":[makeQuery(id+"F4.opExtrude","SWEPT_EDGE",EDGE,{"disambiguationData":[OSD([subQ1,subQ0])]}),makeQuery(id+"F5.opExtrude","SWEPT_EDGE",EDGE,{"disambiguationData":[OSD([subQ1,subQ0])]})]}),makeQuery(id+"F5.opExtrude","CAP_FACE",FACE,{"disambiguationData":[OSD([subQ1,sQuery(id+"F3.wireOp",EDGE,"E3"),sQuery(id+"F3.wireOp",EDGE,"E4"),sQuery(id+"F3.wireOp",EDGE,"E5"),sQuery(id+"F3.wireOp",EDGE,"E6"),sQuery(id+"F3.wireOp",EDGE,"E7"),sQuery(id+"F3.wireOp",EDGE,"E8"),sQuery(id+"F3.wireOp",EDGE,"E9.1.0"),sQuery(id+"F3.wireOp",EDGE,"E9.1.1"),sQuery(id+"F3.wireOp",EDGE,"E9.1.2"),sQuery(id+"F3.wireOp",EDGE,"E9.1.3"),sQuery(id+"F3.wireOp",EDGE,"E9.1.4"),sQuery(id+"F3.wireOp",EDGE,"E9.1.5"),sQuery(id+"F3.wireOp",EDGE,"E9.2.0"),sQuery(id+"F3.wireOp",EDGE,"E9.2.1"),sQuery(id+"F3.wireOp",EDGE,"E9.2.2"),sQuery(id+"F3.wireOp",EDGE,"E9.2.3"),sQuery(id+"F3.wireOp",EDGE,"E9.2.4"),sQuery(id+"F3.wireOp",EDGE,"E9.2.5"),sQuery(id+"F3.wireOp",EDGE,"E9.3.0"),sQuery(id+"F3.wireOp",EDGE,"E9.3.1"),sQuery(id+"F3.wireOp",EDGE,"E9.3.2"),sQuery(id+"F3.wireOp",EDGE,"E9.3.3"),sQuery(id+"F3.wireOp",EDGE,"E9.3.4"),sQuery(id+"F3.wireOp",EDGE,"E9.3.5"),sQuery(id+"F3.wireOp",EDGE,"E9.4.0"),sQuery(id+"F3.wireOp",EDGE,"E9.4.1"),sQuery(id+"F3.wireOp",EDGE,"E9.4.2"),sQuery(id+"F3.wireOp",EDGE,"E9.4.3"),sQuery(id+"F3.wireOp",EDGE,"E9.4.4"),subQ0,sQuery(id+"F3.wireOp",EDGE,"E9.5.0"),sQuery(id+"F3.wireOp",EDGE,"E9.5.1"),sQuery(id+"F3.wireOp",EDGE,"E9.5.2"),sQuery(id+"F3.wireOp",EDGE,"E9.5.3"),sQuery(id+"F3.wireOp",EDGE,"E9.5.4"),sQuery(id+"F3.wireOp",EDGE,"E9.5.5"),sQuery(id+"F3.wireOp",EDGE,"E9.6.0"),sQuery(id+"F3.wireOp",EDGE,"E9.6.1"),sQuery(id+"F3.wireOp",EDGE,"E9.6.2"),sQuery(id+"F3.wireOp",EDGE,"E9.6.3"),sQuery(id+"F3.wireOp",EDGE,"E9.6.4"),sQuery(id+"F3.wireOp",EDGE,"E9.6.5"),sQuery(id+"F3.wireOp",EDGE,"E9.7.0"),sQuery(id+"F3.wireOp",EDGE,"E9.7.1"),sQuery(id+"F3.wireOp",EDGE,"E9.7.2"),sQuery(id+"F3.wireOp",EDGE,"E9.7.3"),sQuery(id+"F3.wireOp",EDGE,"E9.7.4"),sQuery(id+"F3.wireOp",EDGE,"E9.7.5")])],"isStart":false})],"blendedInto":[makeQuery(id+"F5.opExtrude","CAP_FACE",FACE,{"disambiguationData":[OSD([subQ1,sQuery(id+"F3.wireOp",EDGE,"E3"),sQuery(id+"F3.wireOp",EDGE,"E4"),sQuery(id+"F3.wireOp",EDGE,"E5"),sQuery(id+"F3.wireOp",EDGE,"E6"),sQuery(id+"F3.wireOp",EDGE,"E7"),sQuery(id+"F3.wireOp",EDGE,"E8"),sQuery(id+"F3.wireOp",EDGE,"E9.1.0"),sQuery(id+"F3.wireOp",EDGE,"E9.1.1"),sQuery(id+"F3.wireOp",EDGE,"E9.1.2"),sQuery(id+"F3.wireOp",EDGE,"E9.1.3"),sQuery(id+"F3.wireOp",EDGE,"E9.1.4"),sQuery(id+"F3.wireOp",EDGE,"E9.1.5"),sQuery(id+"F3.wireOp",EDGE,"E9.2.0"),sQuery(id+"F3.wireOp",EDGE,"E9.2.1"),sQuery(id+"F3.wireOp",EDGE,"E9.2.2"),sQuery(id+"F3.wireOp",EDGE,"E9.2.3"),sQuery(id+"F3.wireOp",EDGE,"E9.2.4"),sQuery(id+"F3.wireOp",EDGE,"E9.2.5"),sQuery(id+"F3.wireOp",EDGE,"E9.3.0"),sQuery(id+"F3.wireOp",EDGE,"E9.3.1"),sQuery(id+"F3.wireOp",EDGE,"E9.3.2"),sQuery(id+"F3.wireOp",EDGE,"E9.3.3"),sQuery(id+"F3.wireOp",EDGE,"E9.3.4"),sQuery(id+"F3.wireOp",EDGE,"E9.3.5"),sQuery(id+"F3.wireOp",EDGE,"E9.4.0"),sQuery(id+"F3.wireOp",EDGE,"E9.4.1"),sQuery(id+"F3.wireOp",EDGE,"E9.4.2"),sQuery(id+"F3.wireOp",EDGE,"E9.4.3"),sQuery(id+"F3.wireOp",EDGE,"E9.4.4"),subQ0,sQuery(id+"F3.wireOp",EDGE,"E9.5.0"),sQuery(id+"F3.wireOp",EDGE,"E9.5.1"),sQuery(id+"F3.wireOp",EDGE,"E9.5.2"),sQuery(id+"F3.wireOp",EDGE,"E9.5.3"),sQuery(id+"F3.wireOp",EDGE,"E9.5.4"),sQuery(id+"F3.wireOp",EDGE,"E9.5.5"),sQuery(id+"F3.wireOp",EDGE,"E9.6.0"),sQuery(id+"F3.wireOp",EDGE,"E9.6.1"),sQuery(id+"F3.wireOp",EDGE,"E9.6.2"),sQuery(id+"F3.wireOp",EDGE,"E9.6.3"),sQuery(id+"F3.wireOp",EDGE,"E9.6.4"),sQuery(id+"F3.wireOp",EDGE,"E9.6.5"),sQuery(id+"F3.wireOp",EDGE,"E9.7.0"),sQuery(id+"F3.wireOp",EDGE,"E9.7.1"),sQuery(id+"F3.wireOp",EDGE,"E9.7.2"),sQuery(id+"F3.wireOp",EDGE,"E9.7.3"),sQuery(id+"F3.wireOp",EDGE,"E9.7.4"),sQuery(id+"F3.wireOp",EDGE,"E9.7.5")])],"isStart":false})]});}
            var Q10;
            Q10=makeQuery(id+"F5.opExtrude","CAP_EDGE",EDGE,{"disambiguationData":[OSD([sQuery(id+"F3.wireOp",EDGE,"E9.4.5")])],"isStart":false});
            var Q11;
            Q11=makeQuery(id+"F5.opExtrude","CAP_EDGE",EDGE,{"disambiguationData":[OSD([sQuery(id+"F3.wireOp",EDGE,"E9.4.4")])],"isStart":false});
            var Q12;
            Q12=makeQuery(id+"F5.opExtrude","CAP_EDGE",EDGE,{"disambiguationData":[OSD([sQuery(id+"F3.wireOp",EDGE,"E9.4.2"),sQuery(id+"F3.wireOp",EDGE,"E9.4.3")])],"isStart":false});
            var Q13;
            Q13=makeQuery(id+"F5.opExtrude","CAP_EDGE",EDGE,{"disambiguationData":[OSD([sQuery(id+"F3.wireOp",EDGE,"E9.4.1")])],"isStart":false});
            var Q14;
            Q14=makeQuery(id+"F5.opExtrude","CAP_EDGE",EDGE,{"disambiguationData":[OSD([sQuery(id+"F3.wireOp",EDGE,"E9.4.0")])],"isStart":false});
            var Q15;
            {var subQ0=sQuery(id+"F3.wireOp",EDGE,"E9.4.0");var subQ1=sQuery(id+"F3.wireOp",EDGE,"E1");Q15=makeQuery(id+"F8.opFillet","BLEND_EDGE",EDGE,{"blendedFrom":[makeQuery(id+"F5.boolean.opBoolean","MERGE",EDGE,{"derivedFrom":[makeQuery(id+"F4.opExtrude","SWEPT_EDGE",EDGE,{"disambiguationData":[OSD([subQ1,subQ0])]}),makeQuery(id+"F5.opExtrude","SWEPT_EDGE",EDGE,{"disambiguationData":[OSD([subQ1,subQ0])]})]}),makeQuery(id+"F5.opExtrude","CAP_FACE",FACE,{"disambiguationData":[OSD([subQ1,sQuery(id+"F3.wireOp",EDGE,"E3"),sQuery(id+"F3.wireOp",EDGE,"E4"),sQuery(id+"F3.wireOp",EDGE,"E5"),sQuery(id+"F3.wireOp",EDGE,"E6"),sQuery(id+"F3.wireOp",EDGE,"E7"),sQuery(id+"F3.wireOp",EDGE,"E8"),sQuery(id+"F3.wireOp",EDGE,"E9.1.0"),sQuery(id+"F3.wireOp",EDGE,"E9.1.1"),sQuery(id+"F3.wireOp",EDGE,"E9.1.2"),sQuery(id+"F3.wireOp",EDGE,"E9.1.3"),sQuery(id+"F3.wireOp",EDGE,"E9.1.4"),sQuery(id+"F3.wireOp",EDGE,"E9.1.5"),sQuery(id+"F3.wireOp",EDGE,"E9.2.0"),sQuery(id+"F3.wireOp",EDGE,"E9.2.1"),sQuery(id+"F3.wireOp",EDGE,"E9.2.2"),sQuery(id+"F3.wireOp",EDGE,"E9.2.3"),sQuery(id+"F3.wireOp",EDGE,"E9.2.4"),sQuery(id+"F3.wireOp",EDGE,"E9.2.5"),sQuery(id+"F3.wireOp",EDGE,"E9.3.0"),sQuery(id+"F3.wireOp",EDGE,"E9.3.1"),sQuery(id+"F3.wireOp",EDGE,"E9.3.2"),sQuery(id+"F3.wireOp",EDGE,"E9.3.3"),sQuery(id+"F3.wireOp",EDGE,"E9.3.4"),sQuery(id+"F3.wireOp",EDGE,"E9.3.5"),subQ0,sQuery(id+"F3.wireOp",EDGE,"E9.4.1"),sQuery(id+"F3.wireOp",EDGE,"E9.4.2"),sQuery(id+"F3.wireOp",EDGE,"E9.4.3"),sQuery(id+"F3.wireOp",EDGE,"E9.4.4"),sQuery(id+"F3.wireOp",EDGE,"E9.4.5"),sQuery(id+"F3.wireOp",EDGE,"E9.5.0"),sQuery(id+"F3.wireOp",EDGE,"E9.5.1"),sQuery(id+"F3.wireOp",EDGE,"E9.5.2"),sQuery(id+"F3.wireOp",EDGE,"E9.5.3"),sQuery(id+"F3.wireOp",EDGE,"E9.5.4"),sQuery(id+"F3.wireOp",EDGE,"E9.5.5"),sQuery(id+"F3.wireOp",EDGE,"E9.6.0"),sQuery(id+"F3.wireOp",EDGE,"E9.6.1"),sQuery(id+"F3.wireOp",EDGE,"E9.6.2"),sQuery(id+"F3.wireOp",EDGE,"E9.6.3"),sQuery(id+"F3.wireOp",EDGE,"E9.6.4"),sQuery(id+"F3.wireOp",EDGE,"E9.6.5"),sQuery(id+"F3.wireOp",EDGE,"E9.7.0"),sQuery(id+"F3.wireOp",EDGE,"E9.7.1"),sQuery(id+"F3.wireOp",EDGE,"E9.7.2"),sQuery(id+"F3.wireOp",EDGE,"E9.7.3"),sQuery(id+"F3.wireOp",EDGE,"E9.7.4"),sQuery(id+"F3.wireOp",EDGE,"E9.7.5")])],"isStart":false})],"blendedInto":[makeQuery(id+"F5.opExtrude","CAP_FACE",FACE,{"disambiguationData":[OSD([subQ1,sQuery(id+"F3.wireOp",EDGE,"E3"),sQuery(id+"F3.wireOp",EDGE,"E4"),sQuery(id+"F3.wireOp",EDGE,"E5"),sQuery(id+"F3.wireOp",EDGE,"E6"),sQuery(id+"F3.wireOp",EDGE,"E7"),sQuery(id+"F3.wireOp",EDGE,"E8"),sQuery(id+"F3.wireOp",EDGE,"E9.1.0"),sQuery(id+"F3.wireOp",EDGE,"E9.1.1"),sQuery(id+"F3.wireOp",EDGE,"E9.1.2"),sQuery(id+"F3.wireOp",EDGE,"E9.1.3"),sQuery(id+"F3.wireOp",EDGE,"E9.1.4"),sQuery(id+"F3.wireOp",EDGE,"E9.1.5"),sQuery(id+"F3.wireOp",EDGE,"E9.2.0"),sQuery(id+"F3.wireOp",EDGE,"E9.2.1"),sQuery(id+"F3.wireOp",EDGE,"E9.2.2"),sQuery(id+"F3.wireOp",EDGE,"E9.2.3"),sQuery(id+"F3.wireOp",EDGE,"E9.2.4"),sQuery(id+"F3.wireOp",EDGE,"E9.2.5"),sQuery(id+"F3.wireOp",EDGE,"E9.3.0"),sQuery(id+"F3.wireOp",EDGE,"E9.3.1"),sQuery(id+"F3.wireOp",EDGE,"E9.3.2"),sQuery(id+"F3.wireOp",EDGE,"E9.3.3"),sQuery(id+"F3.wireOp",EDGE,"E9.3.4"),sQuery(id+"F3.wireOp",EDGE,"E9.3.5"),subQ0,sQuery(id+"F3.wireOp",EDGE,"E9.4.1"),sQuery(id+"F3.wireOp",EDGE,"E9.4.2"),sQuery(id+"F3.wireOp",EDGE,"E9.4.3"),sQuery(id+"F3.wireOp",EDGE,"E9.4.4"),sQuery(id+"F3.wireOp",EDGE,"E9.4.5"),sQuery(id+"F3.wireOp",EDGE,"E9.5.0"),sQuery(id+"F3.wireOp",EDGE,"E9.5.1"),sQuery(id+"F3.wireOp",EDGE,"E9.5.2"),sQuery(id+"F3.wireOp",EDGE,"E9.5.3"),sQuery(id+"F3.wireOp",EDGE,"E9.5.4"),sQuery(id+"F3.wireOp",EDGE,"E9.5.5"),sQuery(id+"F3.wireOp",EDGE,"E9.6.0"),sQuery(id+"F3.wireOp",EDGE,"E9.6.1"),sQuery(id+"F3.wireOp",EDGE,"E9.6.2"),sQuery(id+"F3.wireOp",EDGE,"E9.6.3"),sQuery(id+"F3.wireOp",EDGE,"E9.6.4"),sQuery(id+"F3.wireOp",EDGE,"E9.6.5"),sQuery(id+"F3.wireOp",EDGE,"E9.7.0"),sQuery(id+"F3.wireOp",EDGE,"E9.7.1"),sQuery(id+"F3.wireOp",EDGE,"E9.7.2"),sQuery(id+"F3.wireOp",EDGE,"E9.7.3"),sQuery(id+"F3.wireOp",EDGE,"E9.7.4"),sQuery(id+"F3.wireOp",EDGE,"E9.7.5")])],"isStart":false})]});}
            var Q16;
            {var subQ0=sQuery(id+"F3.wireOp",EDGE,"E1");var subQ1=makeQuery(id+"F3.imprint","INTERSECT",VERTEX,{"derivedFrom":[subQ0,sQuery(id+"F3.wireOp",EDGE,"E9.5.4")]});var subQ2=makeQuery(id+"F3.imprint","INTERSECT",VERTEX,{"derivedFrom":[subQ0,sQuery(id+"F3.wireOp",EDGE,"E9.4.1")]});Q16=makeQuery(id+"F5.opExtrude","CAP_EDGE",EDGE,{"disambiguationData":[OSD([subQ0]),TDD([makeQuery(id+"F4.opExtrude","CAP_EDGE",EDGE,{"disambiguationData":[OSD([subQ0]),TDD([makeQuery(id+"F3.imprint","IMPRINT",EDGE,{"disambiguationData":[TD([[makeQuery(id+"F3.imprint","INTERSECT",VERTEX,{"derivedFrom":[subQ0,sQuery(id+"F3.wireOp",EDGE,"E9.4.0")]}),-1.0]])],"derivedFrom":subQ0}),makeQuery(id+"F3.imprint","IMPRINT",EDGE,{"disambiguationData":[TD([[subQ2,-1.0]])],"derivedFrom":subQ0}),makeQuery(id+"F3.imprint","IMPRINT",EDGE,{"disambiguationData":[TD([[subQ1,-1.0]])],"derivedFrom":subQ0})])],"isStart":true})])],"isStart":false});}
            var Q17;
            Q17=makeQuery(id+"F5.opExtrude","CAP_EDGE",EDGE,{"disambiguationData":[OSD([sQuery(id+"F3.wireOp",EDGE,"E9.5.4")])],"isStart":false});
            var Q18;
            Q18=makeQuery(id+"F5.opExtrude","CAP_EDGE",EDGE,{"disambiguationData":[OSD([sQuery(id+"F3.wireOp",EDGE,"E9.5.2"),sQuery(id+"F3.wireOp",EDGE,"E9.5.3")])],"isStart":false});
            var Q19;
            Q19=makeQuery(id+"F5.opExtrude","CAP_EDGE",EDGE,{"disambiguationData":[OSD([sQuery(id+"F3.wireOp",EDGE,"E9.5.1")])],"isStart":false});
            var Q20;
            Q20=makeQuery(id+"F5.opExtrude","CAP_EDGE",EDGE,{"disambiguationData":[OSD([sQuery(id+"F3.wireOp",EDGE,"E9.5.0")])],"isStart":false});
            var Q21;
            Q21=makeQuery(id+"F5.opExtrude","CAP_EDGE",EDGE,{"disambiguationData":[OSD([sQuery(id+"F3.wireOp",EDGE,"E9.6.4")])],"isStart":false});
            var Q22;
            Q22=makeQuery(id+"F5.opExtrude","CAP_EDGE",EDGE,{"disambiguationData":[OSD([sQuery(id+"F3.wireOp",EDGE,"E9.6.2"),sQuery(id+"F3.wireOp",EDGE,"E9.6.3")])],"isStart":false});
            var Q23;
            Q23=makeQuery(id+"F5.opExtrude","CAP_EDGE",EDGE,{"disambiguationData":[OSD([sQuery(id+"F3.wireOp",EDGE,"E9.6.1")])],"isStart":false});
            var Q24;
            Q24=makeQuery(id+"F5.opExtrude","CAP_EDGE",EDGE,{"disambiguationData":[OSD([sQuery(id+"F3.wireOp",EDGE,"E9.6.0")])],"isStart":false});
            var Q25;
            {var subQ0=sQuery(id+"F3.wireOp",EDGE,"E9.6.0");var subQ1=sQuery(id+"F3.wireOp",EDGE,"E1");Q25=makeQuery(id+"F8.opFillet","BLEND_EDGE",EDGE,{"blendedFrom":[makeQuery(id+"F5.boolean.opBoolean","MERGE",EDGE,{"derivedFrom":[makeQuery(id+"F4.opExtrude","SWEPT_EDGE",EDGE,{"disambiguationData":[OSD([subQ1,subQ0])]}),makeQuery(id+"F5.opExtrude","SWEPT_EDGE",EDGE,{"disambiguationData":[OSD([subQ1,subQ0])]})]}),makeQuery(id+"F5.opExtrude","CAP_FACE",FACE,{"disambiguationData":[OSD([subQ1,sQuery(id+"F3.wireOp",EDGE,"E3"),sQuery(id+"F3.wireOp",EDGE,"E4"),sQuery(id+"F3.wireOp",EDGE,"E5"),sQuery(id+"F3.wireOp",EDGE,"E6"),sQuery(id+"F3.wireOp",EDGE,"E7"),sQuery(id+"F3.wireOp",EDGE,"E8"),sQuery(id+"F3.wireOp",EDGE,"E9.1.0"),sQuery(id+"F3.wireOp",EDGE,"E9.1.1"),sQuery(id+"F3.wireOp",EDGE,"E9.1.2"),sQuery(id+"F3.wireOp",EDGE,"E9.1.3"),sQuery(id+"F3.wireOp",EDGE,"E9.1.4"),sQuery(id+"F3.wireOp",EDGE,"E9.1.5"),sQuery(id+"F3.wireOp",EDGE,"E9.2.0"),sQuery(id+"F3.wireOp",EDGE,"E9.2.1"),sQuery(id+"F3.wireOp",EDGE,"E9.2.2"),sQuery(id+"F3.wireOp",EDGE,"E9.2.3"),sQuery(id+"F3.wireOp",EDGE,"E9.2.4"),sQuery(id+"F3.wireOp",EDGE,"E9.2.5"),sQuery(id+"F3.wireOp",EDGE,"E9.3.0"),sQuery(id+"F3.wireOp",EDGE,"E9.3.1"),sQuery(id+"F3.wireOp",EDGE,"E9.3.2"),sQuery(id+"F3.wireOp",EDGE,"E9.3.3"),sQuery(id+"F3.wireOp",EDGE,"E9.3.4"),sQuery(id+"F3.wireOp",EDGE,"E9.3.5"),sQuery(id+"F3.wireOp",EDGE,"E9.4.0"),sQuery(id+"F3.wireOp",EDGE,"E9.4.1"),sQuery(id+"F3.wireOp",EDGE,"E9.4.2"),sQuery(id+"F3.wireOp",EDGE,"E9.4.3"),sQuery(id+"F3.wireOp",EDGE,"E9.4.4"),sQuery(id+"F3.wireOp",EDGE,"E9.4.5"),sQuery(id+"F3.wireOp",EDGE,"E9.5.0"),sQuery(id+"F3.wireOp",EDGE,"E9.5.1"),sQuery(id+"F3.wireOp",EDGE,"E9.5.2"),sQuery(id+"F3.wireOp",EDGE,"E9.5.3"),sQuery(id+"F3.wireOp",EDGE,"E9.5.4"),sQuery(id+"F3.wireOp",EDGE,"E9.5.5"),subQ0,sQuery(id+"F3.wireOp",EDGE,"E9.6.1"),sQuery(id+"F3.wireOp",EDGE,"E9.6.2"),sQuery(id+"F3.wireOp",EDGE,"E9.6.3"),sQuery(id+"F3.wireOp",EDGE,"E9.6.4"),sQuery(id+"F3.wireOp",EDGE,"E9.6.5"),sQuery(id+"F3.wireOp",EDGE,"E9.7.0"),sQuery(id+"F3.wireOp",EDGE,"E9.7.1"),sQuery(id+"F3.wireOp",EDGE,"E9.7.2"),sQuery(id+"F3.wireOp",EDGE,"E9.7.3"),sQuery(id+"F3.wireOp",EDGE,"E9.7.4"),sQuery(id+"F3.wireOp",EDGE,"E9.7.5")])],"isStart":false})],"blendedInto":[makeQuery(id+"F5.opExtrude","CAP_FACE",FACE,{"disambiguationData":[OSD([subQ1,sQuery(id+"F3.wireOp",EDGE,"E3"),sQuery(id+"F3.wireOp",EDGE,"E4"),sQuery(id+"F3.wireOp",EDGE,"E5"),sQuery(id+"F3.wireOp",EDGE,"E6"),sQuery(id+"F3.wireOp",EDGE,"E7"),sQuery(id+"F3.wireOp",EDGE,"E8"),sQuery(id+"F3.wireOp",EDGE,"E9.1.0"),sQuery(id+"F3.wireOp",EDGE,"E9.1.1"),sQuery(id+"F3.wireOp",EDGE,"E9.1.2"),sQuery(id+"F3.wireOp",EDGE,"E9.1.3"),sQuery(id+"F3.wireOp",EDGE,"E9.1.4"),sQuery(id+"F3.wireOp",EDGE,"E9.1.5"),sQuery(id+"F3.wireOp",EDGE,"E9.2.0"),sQuery(id+"F3.wireOp",EDGE,"E9.2.1"),sQuery(id+"F3.wireOp",EDGE,"E9.2.2"),sQuery(id+"F3.wireOp",EDGE,"E9.2.3"),sQuery(id+"F3.wireOp",EDGE,"E9.2.4"),sQuery(id+"F3.wireOp",EDGE,"E9.2.5"),sQuery(id+"F3.wireOp",EDGE,"E9.3.0"),sQuery(id+"F3.wireOp",EDGE,"E9.3.1"),sQuery(id+"F3.wireOp",EDGE,"E9.3.2"),sQuery(id+"F3.wireOp",EDGE,"E9.3.3"),sQuery(id+"F3.wireOp",EDGE,"E9.3.4"),sQuery(id+"F3.wireOp",EDGE,"E9.3.5"),sQuery(id+"F3.wireOp",EDGE,"E9.4.0"),sQuery(id+"F3.wireOp",EDGE,"E9.4.1"),sQuery(id+"F3.wireOp",EDGE,"E9.4.2"),sQuery(id+"F3.wireOp",EDGE,"E9.4.3"),sQuery(id+"F3.wireOp",EDGE,"E9.4.4"),sQuery(id+"F3.wireOp",EDGE,"E9.4.5"),sQuery(id+"F3.wireOp",EDGE,"E9.5.0"),sQuery(id+"F3.wireOp",EDGE,"E9.5.1"),sQuery(id+"F3.wireOp",EDGE,"E9.5.2"),sQuery(id+"F3.wireOp",EDGE,"E9.5.3"),sQuery(id+"F3.wireOp",EDGE,"E9.5.4"),sQuery(id+"F3.wireOp",EDGE,"E9.5.5"),subQ0,sQuery(id+"F3.wireOp",EDGE,"E9.6.1"),sQuery(id+"F3.wireOp",EDGE,"E9.6.2"),sQuery(id+"F3.wireOp",EDGE,"E9.6.3"),sQuery(id+"F3.wireOp",EDGE,"E9.6.4"),sQuery(id+"F3.wireOp",EDGE,"E9.6.5"),sQuery(id+"F3.wireOp",EDGE,"E9.7.0"),sQuery(id+"F3.wireOp",EDGE,"E9.7.1"),sQuery(id+"F3.wireOp",EDGE,"E9.7.2"),sQuery(id+"F3.wireOp",EDGE,"E9.7.3"),sQuery(id+"F3.wireOp",EDGE,"E9.7.4"),sQuery(id+"F3.wireOp",EDGE,"E9.7.5")])],"isStart":false})]});}
            var Q26;
            Q26=makeQuery(id+"F5.opExtrude","CAP_EDGE",EDGE,{"disambiguationData":[OSD([sQuery(id+"F3.wireOp",EDGE,"E9.7.4")])],"isStart":false});
            var Q27;
            Q27=makeQuery(id+"F5.opExtrude","CAP_EDGE",EDGE,{"disambiguationData":[OSD([sQuery(id+"F3.wireOp",EDGE,"E9.7.2"),sQuery(id+"F3.wireOp",EDGE,"E9.7.3")])],"isStart":false});
            var Q28;
            Q28=makeQuery(id+"F5.opExtrude","CAP_EDGE",EDGE,{"disambiguationData":[OSD([sQuery(id+"F3.wireOp",EDGE,"E9.7.1")])],"isStart":false});
            var Q29;
            Q29=makeQuery(id+"F5.opExtrude","CAP_EDGE",EDGE,{"disambiguationData":[OSD([sQuery(id+"F3.wireOp",EDGE,"E9.7.0")])],"isStart":false});
            var Q30;
            {var subQ0=sQuery(id+"F3.wireOp",EDGE,"E9.7.0");var subQ1=sQuery(id+"F3.wireOp",EDGE,"E1");Q30=makeQuery(id+"F8.opFillet","BLEND_EDGE",EDGE,{"blendedFrom":[makeQuery(id+"F5.boolean.opBoolean","MERGE",EDGE,{"derivedFrom":[makeQuery(id+"F4.opExtrude","SWEPT_EDGE",EDGE,{"disambiguationData":[OSD([subQ1,subQ0])]}),makeQuery(id+"F5.opExtrude","SWEPT_EDGE",EDGE,{"disambiguationData":[OSD([subQ1,subQ0])]})]}),makeQuery(id+"F5.opExtrude","CAP_FACE",FACE,{"disambiguationData":[OSD([subQ1,sQuery(id+"F3.wireOp",EDGE,"E3"),sQuery(id+"F3.wireOp",EDGE,"E4"),sQuery(id+"F3.wireOp",EDGE,"E5"),sQuery(id+"F3.wireOp",EDGE,"E6"),sQuery(id+"F3.wireOp",EDGE,"E7"),sQuery(id+"F3.wireOp",EDGE,"E8"),sQuery(id+"F3.wireOp",EDGE,"E9.1.0"),sQuery(id+"F3.wireOp",EDGE,"E9.1.1"),sQuery(id+"F3.wireOp",EDGE,"E9.1.2"),sQuery(id+"F3.wireOp",EDGE,"E9.1.3"),sQuery(id+"F3.wireOp",EDGE,"E9.1.4"),sQuery(id+"F3.wireOp",EDGE,"E9.1.5"),sQuery(id+"F3.wireOp",EDGE,"E9.2.0"),sQuery(id+"F3.wireOp",EDGE,"E9.2.1"),sQuery(id+"F3.wireOp",EDGE,"E9.2.2"),sQuery(id+"F3.wireOp",EDGE,"E9.2.3"),sQuery(id+"F3.wireOp",EDGE,"E9.2.4"),sQuery(id+"F3.wireOp",EDGE,"E9.2.5"),sQuery(id+"F3.wireOp",EDGE,"E9.3.0"),sQuery(id+"F3.wireOp",EDGE,"E9.3.1"),sQuery(id+"F3.wireOp",EDGE,"E9.3.2"),sQuery(id+"F3.wireOp",EDGE,"E9.3.3"),sQuery(id+"F3.wireOp",EDGE,"E9.3.4"),sQuery(id+"F3.wireOp",EDGE,"E9.3.5"),sQuery(id+"F3.wireOp",EDGE,"E9.4.0"),sQuery(id+"F3.wireOp",EDGE,"E9.4.1"),sQuery(id+"F3.wireOp",EDGE,"E9.4.2"),sQuery(id+"F3.wireOp",EDGE,"E9.4.3"),sQuery(id+"F3.wireOp",EDGE,"E9.4.4"),sQuery(id+"F3.wireOp",EDGE,"E9.4.5"),sQuery(id+"F3.wireOp",EDGE,"E9.5.0"),sQuery(id+"F3.wireOp",EDGE,"E9.5.1"),sQuery(id+"F3.wireOp",EDGE,"E9.5.2"),sQuery(id+"F3.wireOp",EDGE,"E9.5.3"),sQuery(id+"F3.wireOp",EDGE,"E9.5.4"),sQuery(id+"F3.wireOp",EDGE,"E9.5.5"),sQuery(id+"F3.wireOp",EDGE,"E9.6.0"),sQuery(id+"F3.wireOp",EDGE,"E9.6.1"),sQuery(id+"F3.wireOp",EDGE,"E9.6.2"),sQuery(id+"F3.wireOp",EDGE,"E9.6.3"),sQuery(id+"F3.wireOp",EDGE,"E9.6.4"),sQuery(id+"F3.wireOp",EDGE,"E9.6.5"),subQ0,sQuery(id+"F3.wireOp",EDGE,"E9.7.1"),sQuery(id+"F3.wireOp",EDGE,"E9.7.2"),sQuery(id+"F3.wireOp",EDGE,"E9.7.3"),sQuery(id+"F3.wireOp",EDGE,"E9.7.4"),sQuery(id+"F3.wireOp",EDGE,"E9.7.5")])],"isStart":false})],"blendedInto":[makeQuery(id+"F5.opExtrude","CAP_FACE",FACE,{"disambiguationData":[OSD([subQ1,sQuery(id+"F3.wireOp",EDGE,"E3"),sQuery(id+"F3.wireOp",EDGE,"E4"),sQuery(id+"F3.wireOp",EDGE,"E5"),sQuery(id+"F3.wireOp",EDGE,"E6"),sQuery(id+"F3.wireOp",EDGE,"E7"),sQuery(id+"F3.wireOp",EDGE,"E8"),sQuery(id+"F3.wireOp",EDGE,"E9.1.0"),sQuery(id+"F3.wireOp",EDGE,"E9.1.1"),sQuery(id+"F3.wireOp",EDGE,"E9.1.2"),sQuery(id+"F3.wireOp",EDGE,"E9.1.3"),sQuery(id+"F3.wireOp",EDGE,"E9.1.4"),sQuery(id+"F3.wireOp",EDGE,"E9.1.5"),sQuery(id+"F3.wireOp",EDGE,"E9.2.0"),sQuery(id+"F3.wireOp",EDGE,"E9.2.1"),sQuery(id+"F3.wireOp",EDGE,"E9.2.2"),sQuery(id+"F3.wireOp",EDGE,"E9.2.3"),sQuery(id+"F3.wireOp",EDGE,"E9.2.4"),sQuery(id+"F3.wireOp",EDGE,"E9.2.5"),sQuery(id+"F3.wireOp",EDGE,"E9.3.0"),sQuery(id+"F3.wireOp",EDGE,"E9.3.1"),sQuery(id+"F3.wireOp",EDGE,"E9.3.2"),sQuery(id+"F3.wireOp",EDGE,"E9.3.3"),sQuery(id+"F3.wireOp",EDGE,"E9.3.4"),sQuery(id+"F3.wireOp",EDGE,"E9.3.5"),sQuery(id+"F3.wireOp",EDGE,"E9.4.0"),sQuery(id+"F3.wireOp",EDGE,"E9.4.1"),sQuery(id+"F3.wireOp",EDGE,"E9.4.2"),sQuery(id+"F3.wireOp",EDGE,"E9.4.3"),sQuery(id+"F3.wireOp",EDGE,"E9.4.4"),sQuery(id+"F3.wireOp",EDGE,"E9.4.5"),sQuery(id+"F3.wireOp",EDGE,"E9.5.0"),sQuery(id+"F3.wireOp",EDGE,"E9.5.1"),sQuery(id+"F3.wireOp",EDGE,"E9.5.2"),sQuery(id+"F3.wireOp",EDGE,"E9.5.3"),sQuery(id+"F3.wireOp",EDGE,"E9.5.4"),sQuery(id+"F3.wireOp",EDGE,"E9.5.5"),sQuery(id+"F3.wireOp",EDGE,"E9.6.0"),sQuery(id+"F3.wireOp",EDGE,"E9.6.1"),sQuery(id+"F3.wireOp",EDGE,"E9.6.2"),sQuery(id+"F3.wireOp",EDGE,"E9.6.3"),sQuery(id+"F3.wireOp",EDGE,"E9.6.4"),sQuery(id+"F3.wireOp",EDGE,"E9.6.5"),subQ0,sQuery(id+"F3.wireOp",EDGE,"E9.7.1"),sQuery(id+"F3.wireOp",EDGE,"E9.7.2"),sQuery(id+"F3.wireOp",EDGE,"E9.7.3"),sQuery(id+"F3.wireOp",EDGE,"E9.7.4"),sQuery(id+"F3.wireOp",EDGE,"E9.7.5")])],"isStart":false})]});}
            var Q31;
            Q31=makeQuery(id+"F5.opExtrude","CAP_EDGE",EDGE,{"disambiguationData":[OSD([sQuery(id+"F3.wireOp",EDGE,"E9.2.1")])],"isStart":false});
            var Q32;
            Q32=makeQuery(id+"F5.opExtrude","CAP_EDGE",EDGE,{"disambiguationData":[OSD([sQuery(id+"F3.wireOp",EDGE,"E9.2.2"),sQuery(id+"F3.wireOp",EDGE,"E9.2.3")])],"isStart":false});
            var Q33;
            Q33=makeQuery(id+"F5.opExtrude","CAP_EDGE",EDGE,{"disambiguationData":[OSD([sQuery(id+"F3.wireOp",EDGE,"E9.2.4")])],"isStart":false});
            var Q34;
            Q34=makeQuery(id+"F5.opExtrude","CAP_EDGE",EDGE,{"disambiguationData":[OSD([sQuery(id+"F3.wireOp",EDGE,"E9.2.5")])],"isStart":false});
            var Q35;
            Q35=makeQuery(id+"F5.opExtrude","CAP_EDGE",EDGE,{"disambiguationData":[OSD([sQuery(id+"F3.wireOp",EDGE,"E9.1.1")])],"isStart":false});
            var Q36;
            Q36=makeQuery(id+"F5.opExtrude","CAP_EDGE",EDGE,{"disambiguationData":[OSD([sQuery(id+"F3.wireOp",EDGE,"E9.1.2"),sQuery(id+"F3.wireOp",EDGE,"E9.1.3")])],"isStart":false});
            var Q37;
            Q37=makeQuery(id+"F5.opExtrude","CAP_EDGE",EDGE,{"disambiguationData":[OSD([sQuery(id+"F3.wireOp",EDGE,"E9.1.4")])],"isStart":false});
            var Q38;
            Q38=makeQuery(id+"F5.opExtrude","CAP_EDGE",EDGE,{"disambiguationData":[OSD([sQuery(id+"F3.wireOp",EDGE,"E9.1.5")])],"isStart":false});
            var Q39;
            Q39=makeQuery(id+"F5.opExtrude","CAP_EDGE",EDGE,{"disambiguationData":[OSD([sQuery(id+"F3.wireOp",EDGE,"E4")])],"isStart":false});
            var Q40;
            Q40=makeQuery(id+"F5.opExtrude","CAP_EDGE",EDGE,{"disambiguationData":[OSD([sQuery(id+"F3.wireOp",EDGE,"E3"),sQuery(id+"F3.wireOp",EDGE,"E5")])],"isStart":false});
            var Q41;
            Q41=makeQuery(id+"F5.opExtrude","CAP_EDGE",EDGE,{"disambiguationData":[OSD([sQuery(id+"F3.wireOp",EDGE,"E6")])],"isStart":false});
            fillet(context, id + "F10", {"entities" : qUnion([Q0, Q1, Q2, Q3, Q4, Q5, Q6, Q7, Q8, Q9, Q10, Q11, Q12, Q13, Q14, Q15, Q16, Q17, Q18, Q19, Q20, Q21, Q22, Q23, Q24, Q25, Q26, Q27, Q28, Q29, Q30, Q31, Q32, Q33, Q34, Q35, Q36, Q37, Q38, Q39, Q40, Q41]), "radius" : 0.1 * mm, "tangentPropagation" : true, "allowEdgeOverflow" : false});
        }
        {
            var Q0;
            Q0=makeQuery(id+"F1.opExtrude","CAP_EDGE",EDGE,{"disambiguationData":[OSD([sQuery(id+"F0.wireOp",EDGE,"E0")])],"isStart":true});
            var Q1;
            Q1=makeQuery(id+"F7.opExtrude","CAP_EDGE",EDGE,{"disambiguationData":[OSD([sQuery(id+"F6.wireOp",EDGE,"E10")])],"isStart":false});
            fillet(context, id + "F11", {"entities" : qUnion([Q0, Q1]), "radius" : 0.1 * mm, "tangentPropagation" : true, "allowEdgeOverflow" : false});
        }
        {
            var Q0;
            Q0=makeQuery(id+"F1.opExtrude","CAP_FACE",FACE,{"disambiguationData":[OSD([sQuery(id+"F0.wireOp",EDGE,"E0")])],"isStart":false});
            extrude(context, id + "F12", {"entities" : qUnion([Q0]), "operationType" : NewBodyOperationType.ADD, "depth" : 5 * mm});
        }
    });
